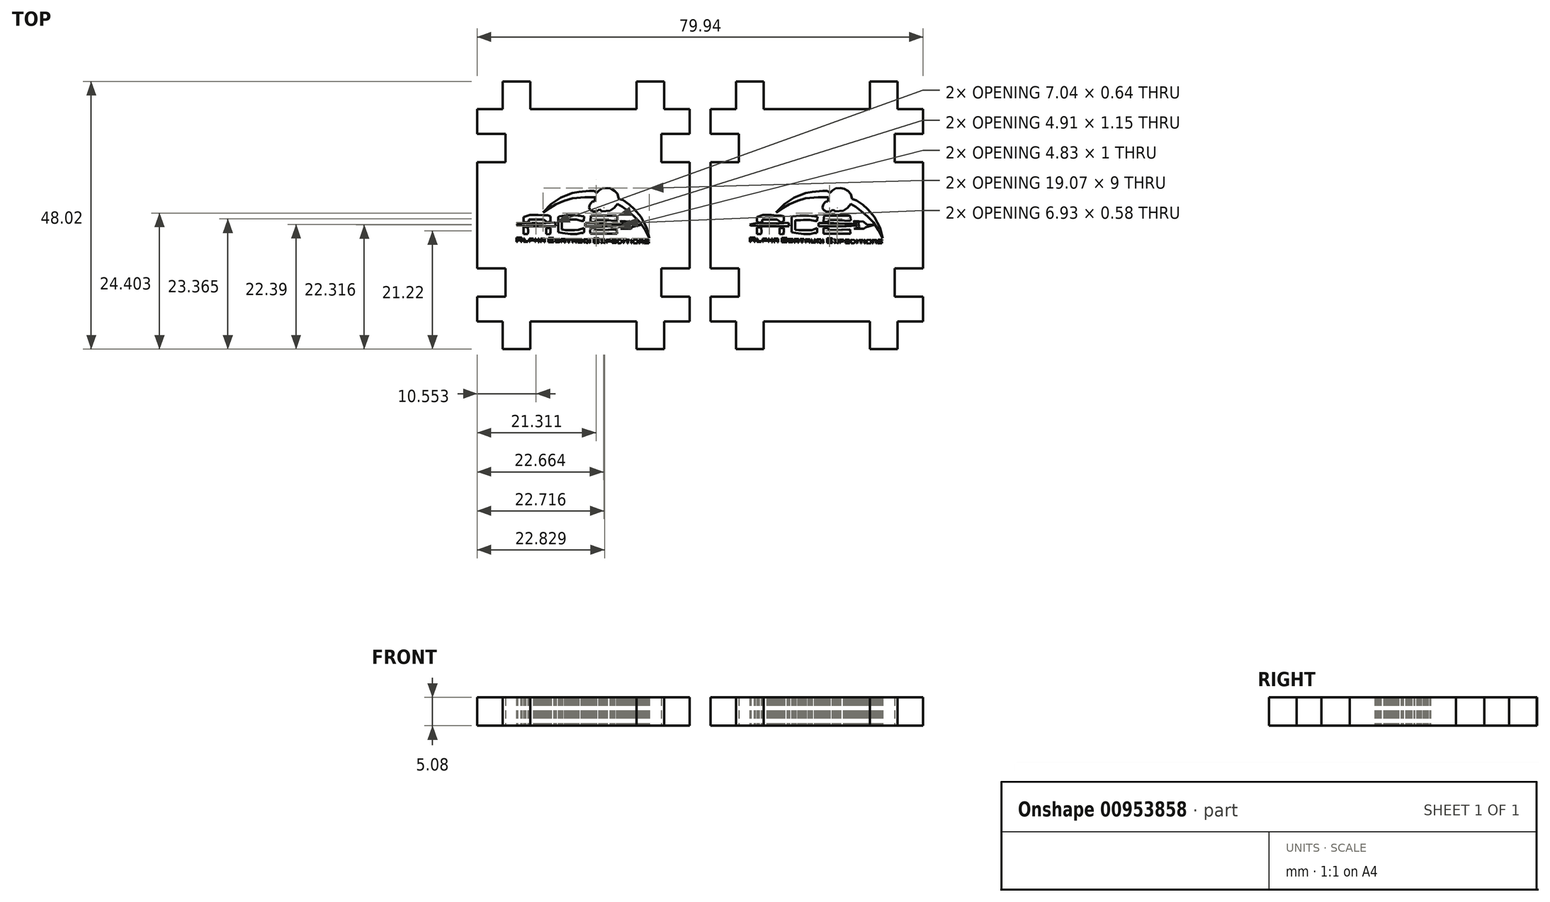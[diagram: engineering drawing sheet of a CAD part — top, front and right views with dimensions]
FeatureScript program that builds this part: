
annotation { "Feature Type Name" : "Feature", "Feature Type Description" : "" }
export const myFeature = defineFeature(function(context is Context, id is Id, definition is map)
    precondition{}
    {
        {
            var Q0;
            Q0=qCreatedBy(makeId("Top.planeOp"),FACE);
            var sketch = newSketch(context, id + "F0", { "sketchPlane" : qUnion([Q0])});
            skLineSegment(sketch, "E0.top", {"start": v(-44, -7.5) * mm, "end": v(-39.42, -7.5) * mm});
            skLineSegment(sketch, "E0.right", {"start": v(-5.9, 30.6) * mm, "end": v(-5.9, -7.5) * mm});
            skPoint(sketch, "E0.middle", {"position": v(-24.95, 11.56) * mm});
            skLineSegment(sketch, "E1", {"start": v(-44, 30.6) * mm, "end": v(-44, 11.56) * mm});
            skLineSegment(sketch, "E2", {"start": v(-44, 11.56) * mm, "end": v(-44, -7.5) * mm});
            skLineSegment(sketch, "E3", {"start": v(-44, 21.08) * mm, "end": v(-38.92, 21.08) * mm});
            skLineSegment(sketch, "E4", {"start": v(-38.92, 21.08) * mm, "end": v(-38.92, 26.16) * mm});
            skLineSegment(sketch, "E5", {"start": v(-38.92, 26.16) * mm, "end": v(-44, 26.16) * mm});
            skLineSegment(sketch, "E6.MirrorCS", {"start": v(-44, 2.03) * mm, "end": v(-38.92, 2.03) * mm});
            skLineSegment(sketch, "E7.MirrorCS", {"start": v(-38.92, 2.03) * mm, "end": v(-38.92, -3.05) * mm});
            skLineSegment(sketch, "E8.MirrorCS", {"start": v(-38.92, -3.05) * mm, "end": v(-44, -3.05) * mm});
            skLineSegment(sketch, "E9.MirrorCS", {"start": v(-10.98, 21.08) * mm, "end": v(-10.98, 26.16) * mm});
            skLineSegment(sketch, "E10.MirrorCS", {"start": v(-10.98, 26.16) * mm, "end": v(-5.9, 26.16) * mm});
            skLineSegment(sketch, "E11.MirrorCS", {"start": v(-5.9, 21.08) * mm, "end": v(-10.98, 21.08) * mm});
            skLineSegment(sketch, "E12.MirrorCS", {"start": v(-5.9, 2.03) * mm, "end": v(-10.98, 2.03) * mm});
            skLineSegment(sketch, "E13.MirrorCS", {"start": v(-10.98, 2.03) * mm, "end": v(-10.98, -3.05) * mm});
            skLineSegment(sketch, "E14.MirrorCS", {"start": v(-10.98, -3.05) * mm, "end": v(-5.9, -3.05) * mm});
            skLineSegment(sketch, "E15", {"start": v(-44, 30.6) * mm, "end": v(-39.42, 30.6) * mm});
            skLineSegment(sketch, "E16", {"start": v(-24.95, 30.6) * mm, "end": v(-15.42, 30.6) * mm});
            skLineSegment(sketch, "E17", {"start": v(-34.47, 30.6) * mm, "end": v(-34.47, 35.56) * mm});
            skLineSegment(sketch, "E18", {"start": v(-34.47, 35.56) * mm, "end": v(-39.42, 35.56) * mm});
            skLineSegment(sketch, "E19", {"start": v(-39.42, 35.56) * mm, "end": v(-39.42, 30.6) * mm});
            skLineSegment(sketch, "E20", {"start": v(-15.42, 30.6) * mm, "end": v(-15.42, 35.56) * mm});
            skLineSegment(sketch, "E21", {"start": v(-15.42, 35.56) * mm, "end": v(-10.47, 35.56) * mm});
            skLineSegment(sketch, "E22", {"start": v(-10.47, 35.56) * mm, "end": v(-10.47, 30.6) * mm});
            skLineSegment(sketch, "E23.MirrorCS", {"start": v(-34.47, -7.5) * mm, "end": v(-34.47, -12.44) * mm});
            skLineSegment(sketch, "E24.MirrorCS", {"start": v(-34.47, -12.44) * mm, "end": v(-39.42, -12.44) * mm});
            skLineSegment(sketch, "E25.MirrorCS", {"start": v(-39.42, -12.44) * mm, "end": v(-39.42, -7.5) * mm});
            skLineSegment(sketch, "E26.MirrorCS", {"start": v(-15.42, -7.5) * mm, "end": v(-15.42, -12.44) * mm});
            skLineSegment(sketch, "E27.MirrorCS", {"start": v(-15.42, -12.44) * mm, "end": v(-10.47, -12.44) * mm});
            skLineSegment(sketch, "E28.MirrorCS", {"start": v(-10.47, -12.44) * mm, "end": v(-10.47, -7.5) * mm});
            skLineSegment(sketch, "E29.trimOffspring", {"start": v(-34.47, 30.6) * mm, "end": v(-24.95, 30.6) * mm});
            skLineSegment(sketch, "E30.trimOffspring", {"start": v(-10.47, 30.6) * mm, "end": v(-5.9, 30.6) * mm});
            skLineSegment(sketch, "E31.trimOffspring", {"start": v(-34.47, -7.5) * mm, "end": v(-15.42, -7.5) * mm});
            skLineSegment(sketch, "E32.trimOffspring", {"start": v(-10.47, -7.5) * mm, "end": v(-5.9, -7.5) * mm});
            skPoint(sketch, "E33.endSnap0", {"position": v(-13.11, 17.66) * mm});
            skLineSegment(sketch, "E34", {"start": v(-35.7, 10.44) * mm, "end": v(-35.7, 11.26) * mm});
            skLineSegment(sketch, "E35", {"start": v(-35.7, 11.26) * mm, "end": v(-34.58, 11.6) * mm});
            skLineSegment(sketch, "E36", {"start": v(-34.58, 11.6) * mm, "end": v(-33.1, 11.6) * mm});
            skLineSegment(sketch, "E37", {"start": v(-33.1, 11.6) * mm, "end": v(-32.18, 11.52) * mm});
            skLineSegment(sketch, "E38", {"start": v(-32.18, 11.52) * mm, "end": v(-31.36, 11.52) * mm});
            skLineSegment(sketch, "E39", {"start": v(-31.36, 11.52) * mm, "end": v(-30.88, 11.38) * mm});
            skLineSegment(sketch, "E40", {"start": v(-30.88, 11.38) * mm, "end": v(-30.88, 10.48) * mm});
            skLineSegment(sketch, "E41", {"start": v(-30.88, 10.48) * mm, "end": v(-31.36, 10.3) * mm});
            skLineSegment(sketch, "E42", {"start": v(-31.36, 10.3) * mm, "end": v(-31.75, 10.57) * mm});
            skLineSegment(sketch, "E43", {"start": v(-31.75, 10.57) * mm, "end": v(-32.06, 10.77) * mm});
            skLineSegment(sketch, "E44", {"start": v(-32.06, 10.77) * mm, "end": v(-34.73, 10.77) * mm});
            skLineSegment(sketch, "E45", {"start": v(-34.73, 10.77) * mm, "end": v(-34.73, 10.38) * mm});
            skLineSegment(sketch, "E46", {"start": v(-34.73, 10.38) * mm, "end": v(-35.32, 10.26) * mm});
            skLineSegment(sketch, "E47", {"start": v(-35.32, 10.26) * mm, "end": v(-35.7, 10.44) * mm});
            skLineSegment(sketch, "E48", {"start": v(-36.97, 9.95) * mm, "end": v(-35.7, 10.17) * mm});
            skLineSegment(sketch, "E49", {"start": v(-35.7, 10.17) * mm, "end": v(-34.75, 10.17) * mm});
            skLineSegment(sketch, "E50", {"start": v(-34.75, 10.17) * mm, "end": v(-33.34, 10.13) * mm});
            skLineSegment(sketch, "E51", {"start": v(-33.34, 10.13) * mm, "end": v(-31.7, 10.13) * mm});
            skLineSegment(sketch, "E52", {"start": v(-31.7, 10.13) * mm, "end": v(-30.06, 10.25) * mm});
            skLineSegment(sketch, "E53", {"start": v(-30.06, 10.25) * mm, "end": v(-29.93, 9.6) * mm});
            skLineSegment(sketch, "E54", {"start": v(-29.93, 9.6) * mm, "end": v(-34.95, 9.6) * mm});
            skLineSegment(sketch, "E55", {"start": v(-34.95, 9.6) * mm, "end": v(-35.99, 9.74) * mm});
            skLineSegment(sketch, "E56", {"start": v(-35.99, 9.74) * mm, "end": v(-36.8, 9.74) * mm});
            skLineSegment(sketch, "E57", {"start": v(-36.8, 9.74) * mm, "end": v(-36.97, 9.95) * mm});
            skLineSegment(sketch, "E58", {"start": v(-35.7, 9.42) * mm, "end": v(-35.7, 8.41) * mm});
            skLineSegment(sketch, "E59", {"start": v(-35.7, 8.41) * mm, "end": v(-35.7, 8.17) * mm});
            skLineSegment(sketch, "E60", {"start": v(-35.7, 8.17) * mm, "end": v(-34.95, 8.17) * mm});
            skLineSegment(sketch, "E61", {"start": v(-34.95, 8.17) * mm, "end": v(-34.84, 8.6) * mm});
            skLineSegment(sketch, "E62", {"start": v(-34.84, 8.6) * mm, "end": v(-34.95, 9.42) * mm});
            skLineSegment(sketch, "E63", {"start": v(-34.95, 9.42) * mm, "end": v(-35.7, 9.42) * mm});
            skLineSegment(sketch, "E64", {"start": v(-31.62, 9.26) * mm, "end": v(-31.62, 8.17) * mm});
            skLineSegment(sketch, "E65", {"start": v(-31.62, 8.17) * mm, "end": v(-31.01, 8.13) * mm});
            skLineSegment(sketch, "E66", {"start": v(-31.01, 8.13) * mm, "end": v(-30.86, 8.48) * mm});
            skLineSegment(sketch, "E67", {"start": v(-30.86, 8.48) * mm, "end": v(-30.86, 9.25) * mm});
            skLineSegment(sketch, "E68", {"start": v(-30.86, 9.25) * mm, "end": v(-31.62, 9.26) * mm});
            skLineSegment(sketch, "E69", {"start": v(-29.46, 11.22) * mm, "end": v(-29.46, 8.52) * mm});
            skLineSegment(sketch, "E70", {"start": v(-29.46, 8.52) * mm, "end": v(-28.7, 8.36) * mm});
            skLineSegment(sketch, "E71", {"start": v(-28.7, 8.36) * mm, "end": v(-27.32, 8.2) * mm});
            skLineSegment(sketch, "E72", {"start": v(-27.32, 8.2) * mm, "end": v(-26.16, 8.2) * mm});
            skLineSegment(sketch, "E73", {"start": v(-26.16, 8.2) * mm, "end": v(-25.39, 8.37) * mm});
            skLineSegment(sketch, "E74", {"start": v(-25.39, 8.37) * mm, "end": v(-24.97, 8.37) * mm});
            skLineSegment(sketch, "E75", {"start": v(-24.97, 8.37) * mm, "end": v(-24.86, 8.64) * mm});
            skLineSegment(sketch, "E76", {"start": v(-24.86, 8.64) * mm, "end": v(-24.86, 9.26) * mm});
            skLineSegment(sketch, "E77", {"start": v(-24.86, 9.26) * mm, "end": v(-25.86, 8.93) * mm});
            skLineSegment(sketch, "E78", {"start": v(-25.86, 8.93) * mm, "end": v(-26.53, 8.87) * mm});
            skLineSegment(sketch, "E79", {"start": v(-26.53, 8.87) * mm, "end": v(-27, 8.87) * mm});
            skLineSegment(sketch, "E80", {"start": v(-27, 8.87) * mm, "end": v(-28.15, 8.87) * mm});
            skLineSegment(sketch, "E81", {"start": v(-28.15, 8.87) * mm, "end": v(-28.8, 8.98) * mm});
            skLineSegment(sketch, "E82", {"start": v(-28.8, 8.98) * mm, "end": v(-28.8, 9.42) * mm});
            skLineSegment(sketch, "E83", {"start": v(-28.8, 9.42) * mm, "end": v(-28.8, 10.22) * mm});
            skLineSegment(sketch, "E84", {"start": v(-28.8, 10.22) * mm, "end": v(-28.8, 10.7) * mm});
            skLineSegment(sketch, "E85", {"start": v(-28.8, 10.7) * mm, "end": v(-27.88, 10.7) * mm});
            skLineSegment(sketch, "E86", {"start": v(-27.88, 10.7) * mm, "end": v(-27.34, 10.76) * mm});
            skLineSegment(sketch, "E87", {"start": v(-27.34, 10.76) * mm, "end": v(-26.2, 10.76) * mm});
            skLineSegment(sketch, "E88", {"start": v(-26.2, 10.76) * mm, "end": v(-25.3, 10.55) * mm});
            skLineSegment(sketch, "E89", {"start": v(-25.3, 10.55) * mm, "end": v(-24.9, 10.55) * mm});
            skLineSegment(sketch, "E90", {"start": v(-24.9, 10.55) * mm, "end": v(-24.8, 11.33) * mm});
            skLineSegment(sketch, "E91", {"start": v(-24.8, 11.33) * mm, "end": v(-26.44, 11.53) * mm});
            skLineSegment(sketch, "E92", {"start": v(-26.44, 11.53) * mm, "end": v(-28, 11.53) * mm});
            skLineSegment(sketch, "E93", {"start": v(-28, 11.53) * mm, "end": v(-29.29, 11.36) * mm});
            skLineSegment(sketch, "E94", {"start": v(-29.29, 11.36) * mm, "end": v(-29.46, 11.22) * mm});
            skLineSegment(sketch, "E95", {"start": v(-24.64, 10.14) * mm, "end": v(-24.64, 9.57) * mm});
            skLineSegment(sketch, "E96", {"start": v(-24.64, 9.57) * mm, "end": v(-19.66, 9.57) * mm});
            skLineSegment(sketch, "E97", {"start": v(-19.66, 9.57) * mm, "end": v(-18.62, 9.67) * mm});
            skLineSegment(sketch, "E98", {"start": v(-18.62, 9.67) * mm, "end": v(-17.7, 9.75) * mm});
            skLineSegment(sketch, "E99", {"start": v(-17.7, 9.75) * mm, "end": v(-17.7, 9.9) * mm});
            skLineSegment(sketch, "E100", {"start": v(-17.7, 9.9) * mm, "end": v(-18.68, 10.05) * mm});
            skLineSegment(sketch, "E101", {"start": v(-18.68, 10.05) * mm, "end": v(-20.12, 10.05) * mm});
            skLineSegment(sketch, "E102", {"start": v(-20.12, 10.05) * mm, "end": v(-21.88, 10.14) * mm});
            skLineSegment(sketch, "E103", {"start": v(-21.88, 10.14) * mm, "end": v(-24.64, 10.14) * mm});
            skLineSegment(sketch, "E104", {"start": v(-23.71, 10.55) * mm, "end": v(-23.63, 11.48) * mm});
            skLineSegment(sketch, "E105", {"start": v(-23.63, 11.48) * mm, "end": v(-19.03, 11.48) * mm});
            skLineSegment(sketch, "E106", {"start": v(-19.03, 11.48) * mm, "end": v(-18.89, 11.33) * mm});
            skLineSegment(sketch, "E107", {"start": v(-18.89, 11.33) * mm, "end": v(-18.83, 10.7) * mm});
            skLineSegment(sketch, "E108", {"start": v(-18.83, 10.7) * mm, "end": v(-19.05, 10.55) * mm});
            skLineSegment(sketch, "E109", {"start": v(-19.05, 10.55) * mm, "end": v(-21.94, 10.7) * mm});
            skLineSegment(sketch, "E110", {"start": v(-21.94, 10.7) * mm, "end": v(-22.76, 10.7) * mm});
            skLineSegment(sketch, "E111", {"start": v(-22.76, 10.7) * mm, "end": v(-22.81, 10.33) * mm});
            skLineSegment(sketch, "E112", {"start": v(-22.81, 10.33) * mm, "end": v(-23.38, 10.33) * mm});
            skLineSegment(sketch, "E113", {"start": v(-23.38, 10.33) * mm, "end": v(-23.74, 10.44) * mm});
            skLineSegment(sketch, "E114", {"start": v(-23.74, 10.44) * mm, "end": v(-23.71, 10.55) * mm});
            skLineSegment(sketch, "E115", {"start": v(-23.71, 9.26) * mm, "end": v(-22.94, 9.26) * mm});
            skLineSegment(sketch, "E116", {"start": v(-22.94, 9.26) * mm, "end": v(-22.8, 8.92) * mm});
            skLineSegment(sketch, "E117", {"start": v(-22.8, 8.92) * mm, "end": v(-22.1, 8.9) * mm});
            skLineSegment(sketch, "E118", {"start": v(-22.1, 8.9) * mm, "end": v(-19, 9) * mm});
            skLineSegment(sketch, "E119", {"start": v(-19, 9) * mm, "end": v(-18.92, 8.26) * mm});
            skLineSegment(sketch, "E120", {"start": v(-18.92, 8.26) * mm, "end": v(-23.47, 8.26) * mm});
            skLineSegment(sketch, "E121", {"start": v(-23.47, 8.26) * mm, "end": v(-23.71, 8.26) * mm});
            skLineSegment(sketch, "E122", {"start": v(-23.71, 8.26) * mm, "end": v(-23.75, 8.65) * mm});
            skLineSegment(sketch, "E123", {"start": v(-23.75, 8.65) * mm, "end": v(-23.71, 9.26) * mm});
            skLineSegment(sketch, "E124", {"start": v(-18.21, 10.55) * mm, "end": v(-16.54, 10.44) * mm});
            skLineSegment(sketch, "E125", {"start": v(-16.54, 10.44) * mm, "end": v(-16, 9.95) * mm});
            skLineSegment(sketch, "E126", {"start": v(-16, 9.95) * mm, "end": v(-14.66, 9.82) * mm});
            skLineSegment(sketch, "E127", {"start": v(-14.66, 9.82) * mm, "end": v(-16.19, 9.42) * mm});
            skLineSegment(sketch, "E128", {"start": v(-16.19, 9.42) * mm, "end": v(-16.47, 9.13) * mm});
            skLineSegment(sketch, "E129", {"start": v(-16.47, 9.13) * mm, "end": v(-18.28, 9.13) * mm});
            skLineSegment(sketch, "E130", {"start": v(-18.28, 9.13) * mm, "end": v(-17.4, 9.42) * mm});
            skLineSegment(sketch, "E131", {"start": v(-17.4, 9.42) * mm, "end": v(-17.3, 9.62) * mm});
            skLineSegment(sketch, "E132", {"start": v(-17.3, 9.62) * mm, "end": v(-17.48, 9.83) * mm});
            skLineSegment(sketch, "E133", {"start": v(-17.48, 9.83) * mm, "end": v(-17.3, 10.04) * mm});
            skLineSegment(sketch, "E134", {"start": v(-17.3, 10.04) * mm, "end": v(-17.66, 10.32) * mm});
            skLineSegment(sketch, "E135", {"start": v(-17.66, 10.32) * mm, "end": v(-18.25, 10.37) * mm});
            skLineSegment(sketch, "E136", {"start": v(-18.25, 10.37) * mm, "end": v(-18.38, 10.44) * mm});
            skLineSegment(sketch, "E137", {"start": v(-18.38, 10.44) * mm, "end": v(-18.21, 10.55) * mm});
            skLineSegment(sketch, "E138", {"start": v(-18.85, 13.59) * mm, "end": v(-17.99, 13.1) * mm});
            skLineSegment(sketch, "E139", {"start": v(-17.99, 13.1) * mm, "end": v(-17, 12.35) * mm});
            skLineSegment(sketch, "E140", {"start": v(-17, 12.35) * mm, "end": v(-15.89, 11.39) * mm});
            skLineSegment(sketch, "E141", {"start": v(-15.89, 11.39) * mm, "end": v(-14.8, 10.3) * mm});
            skLineSegment(sketch, "E142", {"start": v(-14.8, 10.3) * mm, "end": v(-13.88, 8.92) * mm});
            skLineSegment(sketch, "E143", {"start": v(-13.88, 8.92) * mm, "end": v(-13.16, 7.44) * mm});
            skLineSegment(sketch, "E144", {"start": v(-13.16, 7.44) * mm, "end": v(-13.57, 9.26) * mm});
            skLineSegment(sketch, "E145", {"start": v(-13.57, 9.26) * mm, "end": v(-14.1, 10.2) * mm});
            skLineSegment(sketch, "E146", {"start": v(-14.1, 10.2) * mm, "end": v(-14.6, 11.22) * mm});
            skLineSegment(sketch, "E147", {"start": v(-14.6, 11.22) * mm, "end": v(-15.8, 12.65) * mm});
            skLineSegment(sketch, "E148", {"start": v(-15.8, 12.65) * mm, "end": v(-16.72, 13.48) * mm});
            skLineSegment(sketch, "E149", {"start": v(-16.72, 13.48) * mm, "end": v(-17.85, 14.26) * mm});
            skLineSegment(sketch, "E150", {"start": v(-17.85, 14.26) * mm, "end": v(-18.6, 14.48) * mm});
            skLineSegment(sketch, "E151", {"start": v(-18.6, 14.48) * mm, "end": v(-18.85, 13.59) * mm});
            skLineSegment(sketch, "E152", {"start": v(-18.85, 13.59) * mm, "end": v(-19.4, 12.91) * mm});
            skLineSegment(sketch, "E153", {"start": v(-19.4, 12.91) * mm, "end": v(-20.2, 12.4) * mm});
            skLineSegment(sketch, "E154", {"start": v(-20.2, 12.4) * mm, "end": v(-21.65, 12.26) * mm});
            skLineSegment(sketch, "E155", {"start": v(-21.65, 12.26) * mm, "end": v(-22.02, 12.6) * mm});
            skLineSegment(sketch, "E156", {"start": v(-22.02, 12.6) * mm, "end": v(-22.6, 12.22) * mm});
            skLineSegment(sketch, "E157", {"start": v(-22.6, 12.22) * mm, "end": v(-23.18, 12.23) * mm});
            skLineSegment(sketch, "E158", {"start": v(-23.18, 12.23) * mm, "end": v(-23.6, 12.43) * mm});
            skLineSegment(sketch, "E159", {"start": v(-23.6, 12.43) * mm, "end": v(-23.83, 12.65) * mm});
            skLineSegment(sketch, "E160", {"start": v(-23.83, 12.65) * mm, "end": v(-23.94, 12.93) * mm});
            skLineSegment(sketch, "E161", {"start": v(-23.94, 12.93) * mm, "end": v(-23.8, 13.47) * mm});
            skLineSegment(sketch, "E162", {"start": v(-23.8, 13.47) * mm, "end": v(-23.58, 13.76) * mm});
            skLineSegment(sketch, "E163", {"start": v(-23.58, 13.76) * mm, "end": v(-23.4, 14) * mm});
            skLineSegment(sketch, "E164", {"start": v(-23.4, 14) * mm, "end": v(-23.06, 14.05) * mm});
            skLineSegment(sketch, "E165", {"start": v(-23.06, 14.05) * mm, "end": v(-22.6, 13.99) * mm});
            skLineSegment(sketch, "E166", {"start": v(-22.6, 13.99) * mm, "end": v(-22.27, 13.8) * mm});
            skLineSegment(sketch, "E167", {"start": v(-22.27, 13.8) * mm, "end": v(-21.99, 13.38) * mm});
            skLineSegment(sketch, "E168", {"start": v(-21.99, 13.38) * mm, "end": v(-21.95, 13.14) * mm});
            skLineSegment(sketch, "E169", {"start": v(-21.95, 13.14) * mm, "end": v(-21.95, 12.78) * mm});
            skLineSegment(sketch, "E170", {"start": v(-21.95, 12.78) * mm, "end": v(-22.02, 12.6) * mm});
            skLineSegment(sketch, "E171", {"start": v(-22.97, 14.04) * mm, "end": v(-22.9, 14.6) * mm});
            skLineSegment(sketch, "E172", {"start": v(-22.9, 14.6) * mm, "end": v(-22.6, 15.54) * mm});
            skLineSegment(sketch, "E173", {"start": v(-22.6, 15.54) * mm, "end": v(-22.17, 16) * mm});
            skLineSegment(sketch, "E174", {"start": v(-22.17, 16) * mm, "end": v(-21.6, 16.38) * mm});
            skLineSegment(sketch, "E175", {"start": v(-21.6, 16.38) * mm, "end": v(-20.72, 16.45) * mm});
            skLineSegment(sketch, "E176", {"start": v(-20.72, 16.45) * mm, "end": v(-20.06, 16.35) * mm});
            skLineSegment(sketch, "E177", {"start": v(-20.06, 16.35) * mm, "end": v(-19.39, 15.95) * mm});
            skLineSegment(sketch, "E178", {"start": v(-19.39, 15.95) * mm, "end": v(-18.85, 15.4) * mm});
            skLineSegment(sketch, "E179", {"start": v(-18.85, 15.4) * mm, "end": v(-18.65, 14.7) * mm});
            skLineSegment(sketch, "E180", {"start": v(-18.65, 14.7) * mm, "end": v(-18.6, 14.48) * mm});
            skLineSegment(sketch, "E181", {"start": v(-22.6, 15.54) * mm, "end": v(-23.01, 15.94) * mm});
            skLineSegment(sketch, "E182", {"start": v(-23.01, 15.94) * mm, "end": v(-23.87, 15.95) * mm});
            skLineSegment(sketch, "E183", {"start": v(-23.87, 15.95) * mm, "end": v(-25.77, 15.75) * mm});
            skLineSegment(sketch, "E184", {"start": v(-25.77, 15.75) * mm, "end": v(-26.94, 15.54) * mm});
            skLineSegment(sketch, "E185", {"start": v(-26.94, 15.54) * mm, "end": v(-28.04, 15.12) * mm});
            skLineSegment(sketch, "E186", {"start": v(-28.04, 15.12) * mm, "end": v(-29.04, 14.71) * mm});
            skLineSegment(sketch, "E187", {"start": v(-29.04, 14.71) * mm, "end": v(-30.75, 13.59) * mm});
            skLineSegment(sketch, "E188", {"start": v(-30.75, 13.59) * mm, "end": v(-32.04, 12.26) * mm});
            skLineSegment(sketch, "E189", {"start": v(-32.04, 12.26) * mm, "end": v(-32.22, 12.07) * mm});
            skLineSegment(sketch, "E190", {"start": v(-32.22, 12.07) * mm, "end": v(-30.95, 12.9) * mm});
            skLineSegment(sketch, "E191", {"start": v(-30.95, 12.9) * mm, "end": v(-29.88, 13.52) * mm});
            skLineSegment(sketch, "E192", {"start": v(-29.88, 13.52) * mm, "end": v(-28.4, 14.14) * mm});
            skLineSegment(sketch, "E193", {"start": v(-28.4, 14.14) * mm, "end": v(-26.96, 14.6) * mm});
            skLineSegment(sketch, "E194", {"start": v(-26.96, 14.6) * mm, "end": v(-24.7, 14.82) * mm});
            skLineSegment(sketch, "E195", {"start": v(-24.7, 14.82) * mm, "end": v(-22.82, 14.82) * mm});
            skLineSegment(sketch, "E196", {"start": v(-36.97, 6.8) * mm, "end": v(-36.97, 7.57) * mm});
            skLineSegment(sketch, "E197", {"start": v(-36.97, 7.57) * mm, "end": v(-36, 7.57) * mm});
            skLineSegment(sketch, "E198", {"start": v(-36, 7.57) * mm, "end": v(-36, 6.78) * mm});
            skLineSegment(sketch, "E199", {"start": v(-36, 6.78) * mm, "end": v(-36.18, 6.78) * mm});
            skLineSegment(sketch, "E200", {"start": v(-36.18, 6.78) * mm, "end": v(-36.18, 7.1) * mm});
            skLineSegment(sketch, "E201", {"start": v(-36.18, 7.1) * mm, "end": v(-36.77, 7.1) * mm});
            skLineSegment(sketch, "E202", {"start": v(-36.77, 7.1) * mm, "end": v(-36.77, 6.78) * mm});
            skLineSegment(sketch, "E203", {"start": v(-36.77, 6.78) * mm, "end": v(-36.97, 6.8) * mm});
            skLineSegment(sketch, "E204", {"start": v(-36.79, 7.39) * mm, "end": v(-36.79, 7.28) * mm});
            skLineSegment(sketch, "E205", {"start": v(-36.79, 7.28) * mm, "end": v(-36.2, 7.28) * mm});
            skLineSegment(sketch, "E206", {"start": v(-36.2, 7.28) * mm, "end": v(-36.2, 7.39) * mm});
            skLineSegment(sketch, "E207", {"start": v(-36.2, 7.39) * mm, "end": v(-36.79, 7.39) * mm});
            skLineSegment(sketch, "E208", {"start": v(-35.7, 7.39) * mm, "end": v(-35.7, 6.77) * mm});
            skLineSegment(sketch, "E209", {"start": v(-35.7, 6.77) * mm, "end": v(-34.94, 6.77) * mm});
            skLineSegment(sketch, "E210", {"start": v(-34.94, 6.77) * mm, "end": v(-34.94, 6.9) * mm});
            skLineSegment(sketch, "E211", {"start": v(-34.94, 6.9) * mm, "end": v(-35.53, 6.9) * mm});
            skLineSegment(sketch, "E212", {"start": v(-35.53, 6.9) * mm, "end": v(-35.53, 7.39) * mm});
            skLineSegment(sketch, "E213", {"start": v(-35.53, 7.39) * mm, "end": v(-35.7, 7.39) * mm});
            skLineSegment(sketch, "E214", {"start": v(-34.68, 6.8) * mm, "end": v(-34.68, 7.39) * mm});
            skLineSegment(sketch, "E215", {"start": v(-34.68, 7.39) * mm, "end": v(-33.92, 7.39) * mm});
            skLineSegment(sketch, "E216", {"start": v(-33.92, 7.39) * mm, "end": v(-33.92, 7.01) * mm});
            skLineSegment(sketch, "E217", {"start": v(-33.92, 7.01) * mm, "end": v(-34.53, 7.01) * mm});
            skLineSegment(sketch, "E218", {"start": v(-34.53, 7.01) * mm, "end": v(-34.53, 6.8) * mm});
            skLineSegment(sketch, "E219", {"start": v(-34.53, 6.8) * mm, "end": v(-34.68, 6.8) * mm});
            skLineSegment(sketch, "E220", {"start": v(-34.54, 7.26) * mm, "end": v(-34.54, 7.1) * mm});
            skLineSegment(sketch, "E221", {"start": v(-34.54, 7.1) * mm, "end": v(-34.07, 7.1) * mm});
            skLineSegment(sketch, "E222", {"start": v(-34.07, 7.1) * mm, "end": v(-34.07, 7.25) * mm});
            skLineSegment(sketch, "E223", {"start": v(-34.07, 7.25) * mm, "end": v(-34.54, 7.26) * mm});
            skLineSegment(sketch, "E224", {"start": v(-33.67, 7.39) * mm, "end": v(-33.67, 6.8) * mm});
            skLineSegment(sketch, "E225", {"start": v(-33.67, 6.8) * mm, "end": v(-33.51, 6.8) * mm});
            skLineSegment(sketch, "E226", {"start": v(-33.51, 6.8) * mm, "end": v(-33.52, 6.99) * mm});
            skLineSegment(sketch, "E227", {"start": v(-33.52, 6.99) * mm, "end": v(-33.04, 6.99) * mm});
            skLineSegment(sketch, "E228", {"start": v(-33.04, 6.99) * mm, "end": v(-33.06, 6.75) * mm});
            skLineSegment(sketch, "E229", {"start": v(-33.06, 6.75) * mm, "end": v(-32.9, 6.75) * mm});
            skLineSegment(sketch, "E230", {"start": v(-32.9, 6.75) * mm, "end": v(-32.9, 7.39) * mm});
            skLineSegment(sketch, "E231", {"start": v(-32.9, 7.39) * mm, "end": v(-33.08, 7.39) * mm});
            skLineSegment(sketch, "E232", {"start": v(-33.08, 7.39) * mm, "end": v(-33.08, 7.14) * mm});
            skLineSegment(sketch, "E233", {"start": v(-33.08, 7.14) * mm, "end": v(-33.47, 7.14) * mm});
            skLineSegment(sketch, "E234", {"start": v(-33.47, 7.14) * mm, "end": v(-33.47, 7.39) * mm});
            skLineSegment(sketch, "E235", {"start": v(-33.47, 7.39) * mm, "end": v(-33.67, 7.39) * mm});
            skLineSegment(sketch, "E236", {"start": v(-32.65, 6.76) * mm, "end": v(-32.65, 7.39) * mm});
            skLineSegment(sketch, "E237", {"start": v(-32.65, 7.39) * mm, "end": v(-31.88, 7.39) * mm});
            skLineSegment(sketch, "E238", {"start": v(-31.88, 7.39) * mm, "end": v(-31.88, 6.73) * mm});
            skLineSegment(sketch, "E239", {"start": v(-31.88, 6.73) * mm, "end": v(-32.02, 6.73) * mm});
            skLineSegment(sketch, "E240", {"start": v(-32.02, 6.73) * mm, "end": v(-32, 6.96) * mm});
            skLineSegment(sketch, "E241", {"start": v(-32, 6.96) * mm, "end": v(-32.48, 6.96) * mm});
            skLineSegment(sketch, "E242", {"start": v(-32.48, 6.96) * mm, "end": v(-32.47, 6.74) * mm});
            skLineSegment(sketch, "E243", {"start": v(-32.47, 6.74) * mm, "end": v(-32.65, 6.76) * mm});
            skLineSegment(sketch, "E244", {"start": v(-32.48, 7.22) * mm, "end": v(-32.48, 7.1) * mm});
            skLineSegment(sketch, "E245", {"start": v(-32.48, 7.1) * mm, "end": v(-32.04, 7.11) * mm});
            skLineSegment(sketch, "E246", {"start": v(-32.04, 7.11) * mm, "end": v(-32.06, 7.24) * mm});
            skLineSegment(sketch, "E247", {"start": v(-32.06, 7.24) * mm, "end": v(-32.48, 7.22) * mm});
            skLineSegment(sketch, "E248", {"start": v(-31.26, 7.52) * mm, "end": v(-31.26, 6.73) * mm});
            skLineSegment(sketch, "E249", {"start": v(-31.26, 6.73) * mm, "end": v(-30.28, 6.73) * mm});
            skLineSegment(sketch, "E250", {"start": v(-30.28, 6.73) * mm, "end": v(-30.28, 6.89) * mm});
            skLineSegment(sketch, "E251", {"start": v(-30.28, 6.89) * mm, "end": v(-31.01, 6.89) * mm});
            skLineSegment(sketch, "E252", {"start": v(-31.01, 6.89) * mm, "end": v(-31.01, 7.32) * mm});
            skLineSegment(sketch, "E253", {"start": v(-31.01, 7.32) * mm, "end": v(-30.28, 7.32) * mm});
            skLineSegment(sketch, "E254", {"start": v(-30.28, 7.32) * mm, "end": v(-30.28, 7.5) * mm});
            skLineSegment(sketch, "E255", {"start": v(-30.28, 7.5) * mm, "end": v(-31.26, 7.5) * mm});
            skLineSegment(sketch, "E256", {"start": v(-30, 7.32) * mm, "end": v(-30, 6.72) * mm});
            skLineSegment(sketch, "E257", {"start": v(-30, 6.72) * mm, "end": v(-29.25, 6.72) * mm});
            skLineSegment(sketch, "E258", {"start": v(-29.25, 6.72) * mm, "end": v(-29.24, 6.8) * mm});
            skLineSegment(sketch, "E259", {"start": v(-29.24, 6.8) * mm, "end": v(-29.84, 6.8) * mm});
            skLineSegment(sketch, "E260", {"start": v(-29.84, 6.8) * mm, "end": v(-29.84, 6.92) * mm});
            skLineSegment(sketch, "E261", {"start": v(-29.84, 6.92) * mm, "end": v(-29.24, 6.92) * mm});
            skLineSegment(sketch, "E262", {"start": v(-29.24, 6.92) * mm, "end": v(-29.24, 7.07) * mm});
            skLineSegment(sketch, "E263", {"start": v(-29.24, 7.07) * mm, "end": v(-29.83, 7.07) * mm});
            skLineSegment(sketch, "E264", {"start": v(-29.83, 7.07) * mm, "end": v(-29.83, 7.2) * mm});
            skLineSegment(sketch, "E265", {"start": v(-29.83, 7.2) * mm, "end": v(-29.2, 7.2) * mm});
            skLineSegment(sketch, "E266", {"start": v(-29.2, 7.2) * mm, "end": v(-29.2, 7.34) * mm});
            skLineSegment(sketch, "E267", {"start": v(-29.2, 7.34) * mm, "end": v(-30, 7.32) * mm});
            skLineSegment(sketch, "E268", {"start": v(-28.98, 7.32) * mm, "end": v(-28.98, 6.7) * mm});
            skLineSegment(sketch, "E269", {"start": v(-28.98, 6.7) * mm, "end": v(-28.83, 6.7) * mm});
            skLineSegment(sketch, "E270", {"start": v(-28.83, 6.7) * mm, "end": v(-28.81, 7.17) * mm});
            skLineSegment(sketch, "E271", {"start": v(-28.81, 7.17) * mm, "end": v(-28.36, 7.17) * mm});
            skLineSegment(sketch, "E272", {"start": v(-28.36, 7.17) * mm, "end": v(-28.36, 6.66) * mm});
            skLineSegment(sketch, "E273", {"start": v(-28.36, 6.66) * mm, "end": v(-28.21, 6.66) * mm});
            skLineSegment(sketch, "E274", {"start": v(-28.21, 6.66) * mm, "end": v(-28.21, 7.27) * mm});
            skLineSegment(sketch, "E275", {"start": v(-28.21, 7.27) * mm, "end": v(-28.21, 7.32) * mm});
            skLineSegment(sketch, "E276", {"start": v(-28.21, 7.32) * mm, "end": v(-28.98, 7.32) * mm});
            skLineSegment(sketch, "E277", {"start": v(-27.96, 7.3) * mm, "end": v(-27.96, 7.15) * mm});
            skLineSegment(sketch, "E278", {"start": v(-27.96, 7.15) * mm, "end": v(-27.66, 7.15) * mm});
            skLineSegment(sketch, "E279", {"start": v(-27.66, 7.15) * mm, "end": v(-27.66, 6.69) * mm});
            skLineSegment(sketch, "E280", {"start": v(-27.66, 6.69) * mm, "end": v(-27.48, 6.69) * mm});
            skLineSegment(sketch, "E281", {"start": v(-27.48, 6.69) * mm, "end": v(-27.48, 7.17) * mm});
            skLineSegment(sketch, "E282", {"start": v(-27.48, 7.17) * mm, "end": v(-27.2, 7.14) * mm});
            skLineSegment(sketch, "E283", {"start": v(-27.2, 7.14) * mm, "end": v(-27.23, 7.32) * mm});
            skLineSegment(sketch, "E284", {"start": v(-27.23, 7.32) * mm, "end": v(-27.96, 7.3) * mm});
            skLineSegment(sketch, "E285", {"start": v(-26.95, 6.68) * mm, "end": v(-26.95, 7.3) * mm});
            skLineSegment(sketch, "E286", {"start": v(-26.95, 7.3) * mm, "end": v(-26.17, 7.27) * mm});
            skLineSegment(sketch, "E287", {"start": v(-26.17, 7.27) * mm, "end": v(-26.17, 6.66) * mm});
            skLineSegment(sketch, "E288", {"start": v(-26.17, 6.66) * mm, "end": v(-26.36, 6.67) * mm});
            skLineSegment(sketch, "E289", {"start": v(-26.36, 6.67) * mm, "end": v(-26.35, 6.9) * mm});
            skLineSegment(sketch, "E290", {"start": v(-26.35, 6.9) * mm, "end": v(-26.84, 6.9) * mm});
            skLineSegment(sketch, "E291", {"start": v(-26.84, 6.9) * mm, "end": v(-26.83, 6.68) * mm});
            skLineSegment(sketch, "E292", {"start": v(-26.83, 6.68) * mm, "end": v(-26.95, 6.68) * mm});
            skLineSegment(sketch, "E293", {"start": v(-26.79, 7.14) * mm, "end": v(-26.79, 7.03) * mm});
            skLineSegment(sketch, "E294", {"start": v(-26.79, 7.03) * mm, "end": v(-26.35, 7.03) * mm});
            skLineSegment(sketch, "E295", {"start": v(-26.35, 7.03) * mm, "end": v(-26.34, 7.17) * mm});
            skLineSegment(sketch, "E296", {"start": v(-26.34, 7.17) * mm, "end": v(-26.79, 7.14) * mm});
            skLineSegment(sketch, "E297", {"start": v(-25.95, 7.26) * mm, "end": v(-25.95, 6.65) * mm});
            skLineSegment(sketch, "E298", {"start": v(-25.95, 6.65) * mm, "end": v(-25.18, 6.64) * mm});
            skLineSegment(sketch, "E299", {"start": v(-25.18, 6.64) * mm, "end": v(-25.2, 7.3) * mm});
            skLineSegment(sketch, "E300", {"start": v(-25.2, 7.3) * mm, "end": v(-25.31, 7.28) * mm});
            skLineSegment(sketch, "E301", {"start": v(-25.31, 7.28) * mm, "end": v(-25.32, 6.78) * mm});
            skLineSegment(sketch, "E302", {"start": v(-25.32, 6.78) * mm, "end": v(-25.79, 6.78) * mm});
            skLineSegment(sketch, "E303", {"start": v(-25.79, 6.78) * mm, "end": v(-25.8, 7.27) * mm});
            skLineSegment(sketch, "E304", {"start": v(-25.8, 7.27) * mm, "end": v(-25.95, 7.26) * mm});
            skLineSegment(sketch, "E305", {"start": v(-24.92, 7.26) * mm, "end": v(-24.9, 6.68) * mm});
            skLineSegment(sketch, "E306", {"start": v(-24.9, 6.68) * mm, "end": v(-24.73, 6.65) * mm});
            skLineSegment(sketch, "E307", {"start": v(-24.73, 6.65) * mm, "end": v(-24.75, 6.88) * mm});
            skLineSegment(sketch, "E308", {"start": v(-24.75, 6.88) * mm, "end": v(-24.3, 6.62) * mm});
            skLineSegment(sketch, "E309", {"start": v(-24.3, 6.62) * mm, "end": v(-24.15, 6.62) * mm});
            skLineSegment(sketch, "E310", {"start": v(-24.15, 6.62) * mm, "end": v(-24.15, 6.68) * mm});
            skLineSegment(sketch, "E311", {"start": v(-24.15, 6.68) * mm, "end": v(-24.4, 6.84) * mm});
            skLineSegment(sketch, "E312", {"start": v(-24.4, 6.84) * mm, "end": v(-24.15, 6.84) * mm});
            skLineSegment(sketch, "E313", {"start": v(-24.15, 6.84) * mm, "end": v(-24.16, 7.26) * mm});
            skLineSegment(sketch, "E314", {"start": v(-24.16, 7.26) * mm, "end": v(-24.92, 7.26) * mm});
            skLineSegment(sketch, "E315", {"start": v(-24.79, 7.15) * mm, "end": v(-24.78, 7.02) * mm});
            skLineSegment(sketch, "E316", {"start": v(-24.78, 7.02) * mm, "end": v(-24.26, 7.06) * mm});
            skLineSegment(sketch, "E317", {"start": v(-24.26, 7.06) * mm, "end": v(-24.31, 7.14) * mm});
            skLineSegment(sketch, "E318", {"start": v(-24.31, 7.14) * mm, "end": v(-24.79, 7.15) * mm});
            skLineSegment(sketch, "E319", {"start": v(-23.9, 7.26) * mm, "end": v(-23.9, 6.64) * mm});
            skLineSegment(sketch, "E320", {"start": v(-23.9, 6.64) * mm, "end": v(-23.76, 6.62) * mm});
            skLineSegment(sketch, "E321", {"start": v(-23.76, 6.62) * mm, "end": v(-23.78, 7.26) * mm});
            skLineSegment(sketch, "E322", {"start": v(-23.78, 7.26) * mm, "end": v(-23.9, 7.26) * mm});
            skLineSegment(sketch, "E323", {"start": v(-23.9, 7.26) * mm, "end": v(-23.9, 7.26) * mm});
            skLineSegment(sketch, "E324", {"start": v(-23.12, 7.4) * mm, "end": v(-23.1, 6.62) * mm});
            skLineSegment(sketch, "E325", {"start": v(-23.1, 6.62) * mm, "end": v(-22.16, 6.62) * mm});
            skLineSegment(sketch, "E326", {"start": v(-22.16, 6.62) * mm, "end": v(-22.16, 6.82) * mm});
            skLineSegment(sketch, "E327", {"start": v(-22.16, 6.82) * mm, "end": v(-22.9, 6.82) * mm});
            skLineSegment(sketch, "E328", {"start": v(-22.9, 6.82) * mm, "end": v(-22.93, 6.9) * mm});
            skLineSegment(sketch, "E329", {"start": v(-22.93, 6.9) * mm, "end": v(-22.21, 6.92) * mm});
            skLineSegment(sketch, "E330", {"start": v(-22.21, 6.92) * mm, "end": v(-22.17, 7.09) * mm});
            skLineSegment(sketch, "E331", {"start": v(-22.17, 7.09) * mm, "end": v(-22.9, 7.09) * mm});
            skLineSegment(sketch, "E332", {"start": v(-22.9, 7.09) * mm, "end": v(-22.92, 7.26) * mm});
            skLineSegment(sketch, "E333", {"start": v(-22.92, 7.26) * mm, "end": v(-22.15, 7.26) * mm});
            skLineSegment(sketch, "E334", {"start": v(-22.15, 7.26) * mm, "end": v(-22.15, 7.42) * mm});
            skLineSegment(sketch, "E335", {"start": v(-22.15, 7.42) * mm, "end": v(-23.12, 7.4) * mm});
            skLineSegment(sketch, "E336", {"start": v(-21.82, 7.19) * mm, "end": v(-21.61, 7.06) * mm});
            skLineSegment(sketch, "E337", {"start": v(-21.61, 7.06) * mm, "end": v(-21.61, 6.81) * mm});
            skLineSegment(sketch, "E338", {"start": v(-21.61, 6.81) * mm, "end": v(-21.85, 6.62) * mm});
            skLineSegment(sketch, "E339", {"start": v(-21.85, 6.62) * mm, "end": v(-21.71, 6.6) * mm});
            skLineSegment(sketch, "E340", {"start": v(-21.71, 6.6) * mm, "end": v(-21.48, 6.73) * mm});
            skLineSegment(sketch, "E341", {"start": v(-21.48, 6.73) * mm, "end": v(-21.23, 6.57) * mm});
            skLineSegment(sketch, "E342", {"start": v(-21.23, 6.57) * mm, "end": v(-21.1, 6.58) * mm});
            skLineSegment(sketch, "E343", {"start": v(-21.1, 6.58) * mm, "end": v(-21.07, 6.63) * mm});
            skLineSegment(sketch, "E344", {"start": v(-21.07, 6.63) * mm, "end": v(-21.37, 6.8) * mm});
            skLineSegment(sketch, "E345", {"start": v(-21.37, 6.8) * mm, "end": v(-21.38, 7.04) * mm});
            skLineSegment(sketch, "E346", {"start": v(-21.38, 7.04) * mm, "end": v(-21.15, 7.14) * mm});
            skLineSegment(sketch, "E347", {"start": v(-21.15, 7.14) * mm, "end": v(-21.08, 7.2) * mm});
            skLineSegment(sketch, "E348", {"start": v(-21.08, 7.2) * mm, "end": v(-21.11, 7.25) * mm});
            skLineSegment(sketch, "E349", {"start": v(-21.11, 7.25) * mm, "end": v(-21.26, 7.2) * mm});
            skLineSegment(sketch, "E350", {"start": v(-21.26, 7.2) * mm, "end": v(-21.49, 7.1) * mm});
            skLineSegment(sketch, "E351", {"start": v(-21.49, 7.1) * mm, "end": v(-21.73, 7.22) * mm});
            skLineSegment(sketch, "E352", {"start": v(-21.73, 7.22) * mm, "end": v(-21.82, 7.22) * mm});
            skLineSegment(sketch, "E353", {"start": v(-21.82, 7.22) * mm, "end": v(-21.82, 7.19) * mm});
            skLineSegment(sketch, "E354", {"start": v(-20.86, 7.19) * mm, "end": v(-20.84, 6.62) * mm});
            skLineSegment(sketch, "E355", {"start": v(-20.84, 6.62) * mm, "end": v(-20.68, 6.64) * mm});
            skLineSegment(sketch, "E356", {"start": v(-20.68, 6.64) * mm, "end": v(-20.68, 6.84) * mm});
            skLineSegment(sketch, "E357", {"start": v(-20.68, 6.84) * mm, "end": v(-20.1, 6.84) * mm});
            skLineSegment(sketch, "E358", {"start": v(-20.1, 6.84) * mm, "end": v(-20.1, 7.19) * mm});
            skLineSegment(sketch, "E359", {"start": v(-20.1, 7.19) * mm, "end": v(-20.86, 7.19) * mm});
            skLineSegment(sketch, "E360", {"start": v(-20.7, 7.08) * mm, "end": v(-20.7, 6.96) * mm});
            skLineSegment(sketch, "E361", {"start": v(-20.7, 6.96) * mm, "end": v(-20.23, 6.95) * mm});
            skLineSegment(sketch, "E362", {"start": v(-20.23, 6.95) * mm, "end": v(-20.24, 7.1) * mm});
            skLineSegment(sketch, "E363", {"start": v(-20.24, 7.1) * mm, "end": v(-20.7, 7.08) * mm});
            skLineSegment(sketch, "E364", {"start": v(-19.85, 7.14) * mm, "end": v(-19.82, 6.58) * mm});
            skLineSegment(sketch, "E365", {"start": v(-19.82, 6.58) * mm, "end": v(-19.05, 6.58) * mm});
            skLineSegment(sketch, "E366", {"start": v(-19.05, 6.58) * mm, "end": v(-19.07, 6.74) * mm});
            skLineSegment(sketch, "E367", {"start": v(-19.07, 6.74) * mm, "end": v(-19.69, 6.73) * mm});
            skLineSegment(sketch, "E368", {"start": v(-19.69, 6.73) * mm, "end": v(-19.69, 6.83) * mm});
            skLineSegment(sketch, "E369", {"start": v(-19.69, 6.83) * mm, "end": v(-19.06, 6.83) * mm});
            skLineSegment(sketch, "E370", {"start": v(-19.06, 6.83) * mm, "end": v(-19.06, 6.95) * mm});
            skLineSegment(sketch, "E371", {"start": v(-19.06, 6.95) * mm, "end": v(-19.64, 6.94) * mm});
            skLineSegment(sketch, "E372", {"start": v(-19.64, 6.94) * mm, "end": v(-19.65, 7.1) * mm});
            skLineSegment(sketch, "E373", {"start": v(-19.65, 7.1) * mm, "end": v(-19.03, 7.08) * mm});
            skLineSegment(sketch, "E374", {"start": v(-19.03, 7.08) * mm, "end": v(-19.07, 7.2) * mm});
            skLineSegment(sketch, "E375", {"start": v(-19.07, 7.2) * mm, "end": v(-19.87, 7.19) * mm});
            skLineSegment(sketch, "E376", {"start": v(-19.87, 7.19) * mm, "end": v(-19.85, 7.14) * mm});
            skLineSegment(sketch, "E377", {"start": v(-18.82, 7.18) * mm, "end": v(-18.8, 6.52) * mm});
            skLineSegment(sketch, "E378", {"start": v(-18.8, 6.52) * mm, "end": v(-18.26, 6.52) * mm});
            skLineSegment(sketch, "E379", {"start": v(-18.26, 6.52) * mm, "end": v(-18.1, 6.77) * mm});
            skLineSegment(sketch, "E380", {"start": v(-18.1, 6.77) * mm, "end": v(-18.08, 6.95) * mm});
            skLineSegment(sketch, "E381", {"start": v(-18.08, 6.95) * mm, "end": v(-18.23, 7.11) * mm});
            skLineSegment(sketch, "E382", {"start": v(-18.23, 7.11) * mm, "end": v(-18.82, 7.18) * mm});
            skLineSegment(sketch, "E383", {"start": v(-18.68, 7.01) * mm, "end": v(-18.66, 6.73) * mm});
            skLineSegment(sketch, "E384", {"start": v(-18.66, 6.73) * mm, "end": v(-18.48, 6.7) * mm});
            skLineSegment(sketch, "E385", {"start": v(-18.48, 6.7) * mm, "end": v(-18.3, 6.75) * mm});
            skLineSegment(sketch, "E386", {"start": v(-18.3, 6.75) * mm, "end": v(-18.2, 6.84) * mm});
            skLineSegment(sketch, "E387", {"start": v(-18.2, 6.84) * mm, "end": v(-18.26, 7) * mm});
            skLineSegment(sketch, "E388", {"start": v(-18.26, 7) * mm, "end": v(-18.63, 7.06) * mm});
            skLineSegment(sketch, "E389", {"start": v(-18.63, 7.06) * mm, "end": v(-18.68, 7.01) * mm});
            skLineSegment(sketch, "E390", {"start": v(-17.82, 7.15) * mm, "end": v(-17.82, 6.59) * mm});
            skLineSegment(sketch, "E391", {"start": v(-17.82, 6.59) * mm, "end": v(-17.67, 6.57) * mm});
            skLineSegment(sketch, "E392", {"start": v(-17.67, 6.57) * mm, "end": v(-17.67, 7.15) * mm});
            skLineSegment(sketch, "E393", {"start": v(-17.67, 7.15) * mm, "end": v(-17.82, 7.15) * mm});
            skLineSegment(sketch, "E394", {"start": v(-17.4, 7.15) * mm, "end": v(-17.4, 7.06) * mm});
            skLineSegment(sketch, "E395", {"start": v(-17.4, 7.06) * mm, "end": v(-17.13, 7.06) * mm});
            skLineSegment(sketch, "E396", {"start": v(-17.13, 7.06) * mm, "end": v(-17.1, 6.54) * mm});
            skLineSegment(sketch, "E397", {"start": v(-17.1, 6.54) * mm, "end": v(-16.97, 6.54) * mm});
            skLineSegment(sketch, "E398", {"start": v(-16.97, 6.54) * mm, "end": v(-16.97, 7.05) * mm});
            skLineSegment(sketch, "E399", {"start": v(-16.97, 7.05) * mm, "end": v(-16.7, 7.04) * mm});
            skLineSegment(sketch, "E400", {"start": v(-16.7, 7.04) * mm, "end": v(-16.7, 7.18) * mm});
            skLineSegment(sketch, "E401", {"start": v(-16.7, 7.18) * mm, "end": v(-17.4, 7.15) * mm});
            skLineSegment(sketch, "E402", {"start": v(-16.42, 7.15) * mm, "end": v(-16.42, 6.54) * mm});
            skLineSegment(sketch, "E403", {"start": v(-16.42, 6.54) * mm, "end": v(-16.25, 6.54) * mm});
            skLineSegment(sketch, "E404", {"start": v(-16.25, 6.54) * mm, "end": v(-16.23, 7.19) * mm});
            skLineSegment(sketch, "E405", {"start": v(-16.23, 7.19) * mm, "end": v(-16.42, 7.14) * mm});
            skLineSegment(sketch, "E406", {"start": v(-16, 7.15) * mm, "end": v(-16, 6.52) * mm});
            skLineSegment(sketch, "E407", {"start": v(-16, 6.52) * mm, "end": v(-15.25, 6.52) * mm});
            skLineSegment(sketch, "E408", {"start": v(-15.25, 6.52) * mm, "end": v(-15.25, 7.16) * mm});
            skLineSegment(sketch, "E409", {"start": v(-15.25, 7.16) * mm, "end": v(-16, 7.15) * mm});
            skLineSegment(sketch, "E410", {"start": v(-15.84, 7.04) * mm, "end": v(-15.84, 6.66) * mm});
            skLineSegment(sketch, "E411", {"start": v(-15.84, 6.66) * mm, "end": v(-15.41, 6.68) * mm});
            skLineSegment(sketch, "E412", {"start": v(-15.41, 6.68) * mm, "end": v(-15.44, 7.04) * mm});
            skLineSegment(sketch, "E413", {"start": v(-15.44, 7.04) * mm, "end": v(-15.84, 7.04) * mm});
            skLineSegment(sketch, "E414", {"start": v(-15.03, 6.53) * mm, "end": v(-14.82, 6.53) * mm});
            skLineSegment(sketch, "E415", {"start": v(-14.82, 6.53) * mm, "end": v(-14.82, 7.04) * mm});
            skLineSegment(sketch, "E416", {"start": v(-14.82, 7.04) * mm, "end": v(-14.36, 7.01) * mm});
            skLineSegment(sketch, "E417", {"start": v(-14.36, 7.01) * mm, "end": v(-14.36, 6.53) * mm});
            skLineSegment(sketch, "E418", {"start": v(-14.36, 6.53) * mm, "end": v(-14.25, 6.53) * mm});
            skLineSegment(sketch, "E419", {"start": v(-14.25, 6.53) * mm, "end": v(-14.25, 7.13) * mm});
            skLineSegment(sketch, "E420", {"start": v(-14.25, 7.13) * mm, "end": v(-15.01, 7.13) * mm});
            skLineSegment(sketch, "E421", {"start": v(-15.01, 7.13) * mm, "end": v(-15.03, 6.53) * mm});
            skLineSegment(sketch, "E422", {"start": v(-14, 6.63) * mm, "end": v(-14, 6.5) * mm});
            skLineSegment(sketch, "E423", {"start": v(-14, 6.5) * mm, "end": v(-13.24, 6.55) * mm});
            skLineSegment(sketch, "E424", {"start": v(-13.24, 6.55) * mm, "end": v(-13.24, 6.86) * mm});
            skLineSegment(sketch, "E425", {"start": v(-13.24, 6.86) * mm, "end": v(-13.82, 6.91) * mm});
            skLineSegment(sketch, "E426", {"start": v(-13.82, 6.91) * mm, "end": v(-13.82, 7) * mm});
            skLineSegment(sketch, "E427", {"start": v(-13.82, 7) * mm, "end": v(-13.22, 7.04) * mm});
            skLineSegment(sketch, "E428", {"start": v(-13.22, 7.04) * mm, "end": v(-13.22, 7.15) * mm});
            skLineSegment(sketch, "E429", {"start": v(-13.22, 7.15) * mm, "end": v(-13.97, 7.17) * mm});
            skLineSegment(sketch, "E430", {"start": v(-13.97, 7.17) * mm, "end": v(-13.97, 6.77) * mm});
            skLineSegment(sketch, "E431", {"start": v(-13.97, 6.77) * mm, "end": v(-13.43, 6.76) * mm});
            skLineSegment(sketch, "E432", {"start": v(-13.43, 6.76) * mm, "end": v(-13.38, 6.7) * mm});
            skLineSegment(sketch, "E433", {"start": v(-13.38, 6.7) * mm, "end": v(-13.38, 6.65) * mm});
            skLineSegment(sketch, "E434", {"start": v(-13.38, 6.65) * mm, "end": v(-14, 6.63) * mm});
            skLineSegment(sketch, "E435.top", {"start": v(-2.16, -7.5) * mm, "end": v(2.4, -7.5) * mm});
            skLineSegment(sketch, "E435.right", {"start": v(35.94, 30.6) * mm, "end": v(35.94, -7.5) * mm});
            skPoint(sketch, "E435.middle", {"position": v(16.89, 11.54) * mm});
            skLineSegment(sketch, "E436", {"start": v(-2.16, 30.6) * mm, "end": v(-2.16, 11.54) * mm});
            skLineSegment(sketch, "E437", {"start": v(-2.16, 11.54) * mm, "end": v(-2.16, -7.5) * mm});
            skLineSegment(sketch, "E438", {"start": v(-2.16, 21.07) * mm, "end": v(2.92, 21.07) * mm});
            skLineSegment(sketch, "E439", {"start": v(2.92, 21.07) * mm, "end": v(2.92, 26.15) * mm});
            skLineSegment(sketch, "E440", {"start": v(2.92, 26.15) * mm, "end": v(-2.16, 26.15) * mm});
            skLineSegment(sketch, "E441.MirrorCS", {"start": v(-2.16, 2.02) * mm, "end": v(2.92, 2.02) * mm});
            skLineSegment(sketch, "E442.MirrorCS", {"start": v(2.92, 2.02) * mm, "end": v(2.92, -3.06) * mm});
            skLineSegment(sketch, "E443.MirrorCS", {"start": v(2.92, -3.06) * mm, "end": v(-2.16, -3.06) * mm});
            skLineSegment(sketch, "E444.MirrorCS", {"start": v(30.86, 21.07) * mm, "end": v(30.86, 26.15) * mm});
            skLineSegment(sketch, "E445.MirrorCS", {"start": v(30.86, 26.15) * mm, "end": v(35.94, 26.15) * mm});
            skLineSegment(sketch, "E446.MirrorCS", {"start": v(35.94, 21.07) * mm, "end": v(30.86, 21.07) * mm});
            skLineSegment(sketch, "E447.MirrorCS", {"start": v(35.94, 2.02) * mm, "end": v(30.86, 2.02) * mm});
            skLineSegment(sketch, "E448.MirrorCS", {"start": v(30.86, 2.02) * mm, "end": v(30.86, -3.06) * mm});
            skLineSegment(sketch, "E449.MirrorCS", {"start": v(30.86, -3.06) * mm, "end": v(35.94, -3.06) * mm});
            skLineSegment(sketch, "E450", {"start": v(-2.16, 30.6) * mm, "end": v(2.4, 30.6) * mm});
            skLineSegment(sketch, "E451", {"start": v(16.89, 30.6) * mm, "end": v(26.41, 30.6) * mm});
            skLineSegment(sketch, "E452", {"start": v(7.36, 30.6) * mm, "end": v(7.36, 35.55) * mm});
            skLineSegment(sketch, "E453", {"start": v(7.36, 35.55) * mm, "end": v(2.4, 35.55) * mm});
            skLineSegment(sketch, "E454", {"start": v(2.4, 35.55) * mm, "end": v(2.4, 30.6) * mm});
            skLineSegment(sketch, "E455", {"start": v(26.41, 30.6) * mm, "end": v(26.41, 35.55) * mm});
            skLineSegment(sketch, "E456", {"start": v(26.41, 35.55) * mm, "end": v(31.37, 35.55) * mm});
            skLineSegment(sketch, "E457", {"start": v(31.37, 35.55) * mm, "end": v(31.37, 30.6) * mm});
            skLineSegment(sketch, "E458.MirrorCS", {"start": v(7.36, -7.5) * mm, "end": v(7.36, -12.46) * mm});
            skLineSegment(sketch, "E459.MirrorCS", {"start": v(7.36, -12.46) * mm, "end": v(2.4, -12.46) * mm});
            skLineSegment(sketch, "E460.MirrorCS", {"start": v(2.4, -12.46) * mm, "end": v(2.4, -7.5) * mm});
            skLineSegment(sketch, "E461.MirrorCS", {"start": v(26.41, -7.5) * mm, "end": v(26.41, -12.46) * mm});
            skLineSegment(sketch, "E462.MirrorCS", {"start": v(26.41, -12.46) * mm, "end": v(31.37, -12.46) * mm});
            skLineSegment(sketch, "E463.MirrorCS", {"start": v(31.37, -12.46) * mm, "end": v(31.37, -7.5) * mm});
            skLineSegment(sketch, "E464.trimOffspring", {"start": v(7.36, 30.6) * mm, "end": v(16.89, 30.6) * mm});
            skLineSegment(sketch, "E465.trimOffspring", {"start": v(31.37, 30.6) * mm, "end": v(35.94, 30.6) * mm});
            skLineSegment(sketch, "E466.trimOffspring", {"start": v(7.36, -7.5) * mm, "end": v(26.41, -7.5) * mm});
            skLineSegment(sketch, "E467.trimOffspring", {"start": v(31.37, -7.5) * mm, "end": v(35.94, -7.5) * mm});
            skPoint(sketch, "E468.endSnap0", {"position": v(28.72, 17.65) * mm});
            skLineSegment(sketch, "E469", {"start": v(6.13, 10.42) * mm, "end": v(6.13, 11.25) * mm});
            skLineSegment(sketch, "E470", {"start": v(6.13, 11.25) * mm, "end": v(7.26, 11.6) * mm});
            skLineSegment(sketch, "E471", {"start": v(7.26, 11.6) * mm, "end": v(8.73, 11.6) * mm});
            skLineSegment(sketch, "E472", {"start": v(8.73, 11.6) * mm, "end": v(9.66, 11.5) * mm});
            skLineSegment(sketch, "E473", {"start": v(9.66, 11.5) * mm, "end": v(10.47, 11.5) * mm});
            skLineSegment(sketch, "E474", {"start": v(10.47, 11.5) * mm, "end": v(10.95, 11.37) * mm});
            skLineSegment(sketch, "E475", {"start": v(10.95, 11.37) * mm, "end": v(10.95, 10.46) * mm});
            skLineSegment(sketch, "E476", {"start": v(10.95, 10.46) * mm, "end": v(10.47, 10.29) * mm});
            skLineSegment(sketch, "E477", {"start": v(10.47, 10.29) * mm, "end": v(10.08, 10.55) * mm});
            skLineSegment(sketch, "E478", {"start": v(10.08, 10.55) * mm, "end": v(9.78, 10.76) * mm});
            skLineSegment(sketch, "E479", {"start": v(9.78, 10.76) * mm, "end": v(7.1, 10.76) * mm});
            skLineSegment(sketch, "E480", {"start": v(7.1, 10.76) * mm, "end": v(7.1, 10.37) * mm});
            skLineSegment(sketch, "E481", {"start": v(7.1, 10.37) * mm, "end": v(6.52, 10.25) * mm});
            skLineSegment(sketch, "E482", {"start": v(6.52, 10.25) * mm, "end": v(6.13, 10.42) * mm});
            skLineSegment(sketch, "E483", {"start": v(4.87, 9.93) * mm, "end": v(6.13, 10.16) * mm});
            skLineSegment(sketch, "E484", {"start": v(6.13, 10.16) * mm, "end": v(7.08, 10.16) * mm});
            skLineSegment(sketch, "E485", {"start": v(7.08, 10.16) * mm, "end": v(8.5, 10.12) * mm});
            skLineSegment(sketch, "E486", {"start": v(8.5, 10.12) * mm, "end": v(10.13, 10.12) * mm});
            skLineSegment(sketch, "E487", {"start": v(10.13, 10.12) * mm, "end": v(11.78, 10.24) * mm});
            skLineSegment(sketch, "E488", {"start": v(11.78, 10.24) * mm, "end": v(11.9, 9.6) * mm});
            skLineSegment(sketch, "E489", {"start": v(11.9, 9.6) * mm, "end": v(6.89, 9.6) * mm});
            skLineSegment(sketch, "E490", {"start": v(6.89, 9.6) * mm, "end": v(5.84, 9.72) * mm});
            skLineSegment(sketch, "E491", {"start": v(5.84, 9.72) * mm, "end": v(5.04, 9.72) * mm});
            skLineSegment(sketch, "E492", {"start": v(5.04, 9.72) * mm, "end": v(4.87, 9.93) * mm});
            skLineSegment(sketch, "E493", {"start": v(6.13, 9.4) * mm, "end": v(6.13, 8.4) * mm});
            skLineSegment(sketch, "E494", {"start": v(6.13, 8.4) * mm, "end": v(6.13, 8.16) * mm});
            skLineSegment(sketch, "E495", {"start": v(6.13, 8.16) * mm, "end": v(6.89, 8.16) * mm});
            skLineSegment(sketch, "E496", {"start": v(6.89, 8.16) * mm, "end": v(7, 8.58) * mm});
            skLineSegment(sketch, "E497", {"start": v(7, 8.58) * mm, "end": v(6.89, 9.4) * mm});
            skLineSegment(sketch, "E498", {"start": v(6.89, 9.4) * mm, "end": v(6.13, 9.4) * mm});
            skLineSegment(sketch, "E499", {"start": v(10.21, 9.25) * mm, "end": v(10.21, 8.16) * mm});
            skLineSegment(sketch, "E500", {"start": v(10.21, 8.16) * mm, "end": v(10.82, 8.12) * mm});
            skLineSegment(sketch, "E501", {"start": v(10.82, 8.12) * mm, "end": v(10.97, 8.46) * mm});
            skLineSegment(sketch, "E502", {"start": v(10.97, 8.46) * mm, "end": v(10.97, 9.24) * mm});
            skLineSegment(sketch, "E503", {"start": v(10.97, 9.24) * mm, "end": v(10.21, 9.25) * mm});
            skLineSegment(sketch, "E504", {"start": v(12.38, 11.2) * mm, "end": v(12.38, 8.5) * mm});
            skLineSegment(sketch, "E505", {"start": v(12.38, 8.5) * mm, "end": v(13.14, 8.35) * mm});
            skLineSegment(sketch, "E506", {"start": v(13.14, 8.35) * mm, "end": v(14.52, 8.18) * mm});
            skLineSegment(sketch, "E507", {"start": v(14.52, 8.18) * mm, "end": v(15.68, 8.18) * mm});
            skLineSegment(sketch, "E508", {"start": v(15.68, 8.18) * mm, "end": v(16.45, 8.36) * mm});
            skLineSegment(sketch, "E509", {"start": v(16.45, 8.36) * mm, "end": v(16.87, 8.36) * mm});
            skLineSegment(sketch, "E510", {"start": v(16.87, 8.36) * mm, "end": v(16.97, 8.63) * mm});
            skLineSegment(sketch, "E511", {"start": v(16.97, 8.63) * mm, "end": v(16.97, 9.25) * mm});
            skLineSegment(sketch, "E512", {"start": v(16.97, 9.25) * mm, "end": v(15.97, 8.91) * mm});
            skLineSegment(sketch, "E513", {"start": v(15.97, 8.91) * mm, "end": v(15.3, 8.86) * mm});
            skLineSegment(sketch, "E514", {"start": v(15.3, 8.86) * mm, "end": v(14.83, 8.86) * mm});
            skLineSegment(sketch, "E515", {"start": v(14.83, 8.86) * mm, "end": v(13.68, 8.86) * mm});
            skLineSegment(sketch, "E516", {"start": v(13.68, 8.86) * mm, "end": v(13.03, 8.97) * mm});
            skLineSegment(sketch, "E517", {"start": v(13.03, 8.97) * mm, "end": v(13.03, 9.4) * mm});
            skLineSegment(sketch, "E518", {"start": v(13.03, 9.4) * mm, "end": v(13.03, 10.2) * mm});
            skLineSegment(sketch, "E519", {"start": v(13.03, 10.2) * mm, "end": v(13.03, 10.68) * mm});
            skLineSegment(sketch, "E520", {"start": v(13.03, 10.68) * mm, "end": v(13.95, 10.68) * mm});
            skLineSegment(sketch, "E521", {"start": v(13.95, 10.68) * mm, "end": v(14.49, 10.75) * mm});
            skLineSegment(sketch, "E522", {"start": v(14.49, 10.75) * mm, "end": v(15.62, 10.75) * mm});
            skLineSegment(sketch, "E523", {"start": v(15.62, 10.75) * mm, "end": v(16.54, 10.53) * mm});
            skLineSegment(sketch, "E524", {"start": v(16.54, 10.53) * mm, "end": v(16.93, 10.53) * mm});
            skLineSegment(sketch, "E525", {"start": v(16.93, 10.53) * mm, "end": v(17.03, 11.31) * mm});
            skLineSegment(sketch, "E526", {"start": v(17.03, 11.31) * mm, "end": v(15.4, 11.51) * mm});
            skLineSegment(sketch, "E527", {"start": v(15.4, 11.51) * mm, "end": v(13.84, 11.51) * mm});
            skLineSegment(sketch, "E528", {"start": v(13.84, 11.51) * mm, "end": v(12.55, 11.34) * mm});
            skLineSegment(sketch, "E529", {"start": v(12.55, 11.34) * mm, "end": v(12.38, 11.2) * mm});
            skLineSegment(sketch, "E530", {"start": v(17.2, 10.13) * mm, "end": v(17.2, 9.55) * mm});
            skLineSegment(sketch, "E531", {"start": v(17.2, 9.55) * mm, "end": v(22.17, 9.55) * mm});
            skLineSegment(sketch, "E532", {"start": v(22.17, 9.55) * mm, "end": v(23.22, 9.65) * mm});
            skLineSegment(sketch, "E533", {"start": v(23.22, 9.65) * mm, "end": v(24.13, 9.74) * mm});
            skLineSegment(sketch, "E534", {"start": v(24.13, 9.74) * mm, "end": v(24.13, 9.88) * mm});
            skLineSegment(sketch, "E535", {"start": v(24.13, 9.88) * mm, "end": v(23.15, 10.03) * mm});
            skLineSegment(sketch, "E536", {"start": v(23.15, 10.03) * mm, "end": v(21.72, 10.03) * mm});
            skLineSegment(sketch, "E537", {"start": v(21.72, 10.03) * mm, "end": v(19.96, 10.13) * mm});
            skLineSegment(sketch, "E538", {"start": v(19.96, 10.13) * mm, "end": v(17.2, 10.13) * mm});
            skLineSegment(sketch, "E539", {"start": v(18.12, 10.53) * mm, "end": v(18.2, 11.47) * mm});
            skLineSegment(sketch, "E540", {"start": v(18.2, 11.47) * mm, "end": v(22.8, 11.47) * mm});
            skLineSegment(sketch, "E541", {"start": v(22.8, 11.47) * mm, "end": v(22.94, 11.31) * mm});
            skLineSegment(sketch, "E542", {"start": v(22.94, 11.31) * mm, "end": v(23, 10.69) * mm});
            skLineSegment(sketch, "E543", {"start": v(23, 10.69) * mm, "end": v(22.78, 10.53) * mm});
            skLineSegment(sketch, "E544", {"start": v(22.78, 10.53) * mm, "end": v(19.9, 10.7) * mm});
            skLineSegment(sketch, "E545", {"start": v(19.9, 10.7) * mm, "end": v(19.08, 10.7) * mm});
            skLineSegment(sketch, "E546", {"start": v(19.08, 10.7) * mm, "end": v(19.02, 10.31) * mm});
            skLineSegment(sketch, "E547", {"start": v(19.02, 10.31) * mm, "end": v(18.46, 10.31) * mm});
            skLineSegment(sketch, "E548", {"start": v(18.46, 10.31) * mm, "end": v(18.1, 10.42) * mm});
            skLineSegment(sketch, "E549", {"start": v(18.1, 10.42) * mm, "end": v(18.12, 10.53) * mm});
            skLineSegment(sketch, "E550", {"start": v(18.12, 9.25) * mm, "end": v(18.9, 9.25) * mm});
            skLineSegment(sketch, "E551", {"start": v(18.9, 9.25) * mm, "end": v(19.04, 8.9) * mm});
            skLineSegment(sketch, "E552", {"start": v(19.04, 8.9) * mm, "end": v(19.72, 8.88) * mm});
            skLineSegment(sketch, "E553", {"start": v(19.72, 8.88) * mm, "end": v(22.84, 9) * mm});
            skLineSegment(sketch, "E554", {"start": v(22.84, 9) * mm, "end": v(22.91, 8.24) * mm});
            skLineSegment(sketch, "E555", {"start": v(22.91, 8.24) * mm, "end": v(18.37, 8.24) * mm});
            skLineSegment(sketch, "E556", {"start": v(18.37, 8.24) * mm, "end": v(18.12, 8.24) * mm});
            skLineSegment(sketch, "E557", {"start": v(18.12, 8.24) * mm, "end": v(18.08, 8.64) * mm});
            skLineSegment(sketch, "E558", {"start": v(18.08, 8.64) * mm, "end": v(18.12, 9.25) * mm});
            skLineSegment(sketch, "E559", {"start": v(23.62, 10.53) * mm, "end": v(25.3, 10.42) * mm});
            skLineSegment(sketch, "E560", {"start": v(25.3, 10.42) * mm, "end": v(25.83, 9.93) * mm});
            skLineSegment(sketch, "E561", {"start": v(25.83, 9.93) * mm, "end": v(27.18, 9.8) * mm});
            skLineSegment(sketch, "E562", {"start": v(27.18, 9.8) * mm, "end": v(25.65, 9.4) * mm});
            skLineSegment(sketch, "E563", {"start": v(25.65, 9.4) * mm, "end": v(25.36, 9.11) * mm});
            skLineSegment(sketch, "E564", {"start": v(25.36, 9.11) * mm, "end": v(23.55, 9.11) * mm});
            skLineSegment(sketch, "E565", {"start": v(23.55, 9.11) * mm, "end": v(24.42, 9.4) * mm});
            skLineSegment(sketch, "E566", {"start": v(24.42, 9.4) * mm, "end": v(24.52, 9.6) * mm});
            skLineSegment(sketch, "E567", {"start": v(24.52, 9.6) * mm, "end": v(24.36, 9.81) * mm});
            skLineSegment(sketch, "E568", {"start": v(24.36, 9.81) * mm, "end": v(24.52, 10.02) * mm});
            skLineSegment(sketch, "E569", {"start": v(24.52, 10.02) * mm, "end": v(24.17, 10.3) * mm});
            skLineSegment(sketch, "E570", {"start": v(24.17, 10.3) * mm, "end": v(23.59, 10.36) * mm});
            skLineSegment(sketch, "E571", {"start": v(23.59, 10.36) * mm, "end": v(23.45, 10.42) * mm});
            skLineSegment(sketch, "E572", {"start": v(23.45, 10.42) * mm, "end": v(23.62, 10.53) * mm});
            skLineSegment(sketch, "E573", {"start": v(22.99, 13.57) * mm, "end": v(23.85, 13.08) * mm});
            skLineSegment(sketch, "E574", {"start": v(23.85, 13.08) * mm, "end": v(24.83, 12.33) * mm});
            skLineSegment(sketch, "E575", {"start": v(24.83, 12.33) * mm, "end": v(25.95, 11.37) * mm});
            skLineSegment(sketch, "E576", {"start": v(25.95, 11.37) * mm, "end": v(27.04, 10.28) * mm});
            skLineSegment(sketch, "E577", {"start": v(27.04, 10.28) * mm, "end": v(27.95, 8.9) * mm});
            skLineSegment(sketch, "E578", {"start": v(27.95, 8.9) * mm, "end": v(28.68, 7.43) * mm});
            skLineSegment(sketch, "E579", {"start": v(28.68, 7.43) * mm, "end": v(28.27, 9.25) * mm});
            skLineSegment(sketch, "E580", {"start": v(28.27, 9.25) * mm, "end": v(27.73, 10.19) * mm});
            skLineSegment(sketch, "E581", {"start": v(27.73, 10.19) * mm, "end": v(27.24, 11.2) * mm});
            skLineSegment(sketch, "E582", {"start": v(27.24, 11.2) * mm, "end": v(26.02, 12.64) * mm});
            skLineSegment(sketch, "E583", {"start": v(26.02, 12.64) * mm, "end": v(25.11, 13.46) * mm});
            skLineSegment(sketch, "E584", {"start": v(25.11, 13.46) * mm, "end": v(23.98, 14.25) * mm});
            skLineSegment(sketch, "E585", {"start": v(23.98, 14.25) * mm, "end": v(23.23, 14.47) * mm});
            skLineSegment(sketch, "E586", {"start": v(23.23, 14.47) * mm, "end": v(22.99, 13.57) * mm});
            skLineSegment(sketch, "E587", {"start": v(22.99, 13.57) * mm, "end": v(22.43, 12.9) * mm});
            skLineSegment(sketch, "E588", {"start": v(22.43, 12.9) * mm, "end": v(21.64, 12.38) * mm});
            skLineSegment(sketch, "E589", {"start": v(21.64, 12.38) * mm, "end": v(20.18, 12.24) * mm});
            skLineSegment(sketch, "E590", {"start": v(20.18, 12.24) * mm, "end": v(19.8, 12.58) * mm});
            skLineSegment(sketch, "E591", {"start": v(19.8, 12.58) * mm, "end": v(19.24, 12.2) * mm});
            skLineSegment(sketch, "E592", {"start": v(19.24, 12.2) * mm, "end": v(18.65, 12.22) * mm});
            skLineSegment(sketch, "E593", {"start": v(18.65, 12.22) * mm, "end": v(18.23, 12.41) * mm});
            skLineSegment(sketch, "E594", {"start": v(18.23, 12.41) * mm, "end": v(18, 12.64) * mm});
            skLineSegment(sketch, "E595", {"start": v(18, 12.64) * mm, "end": v(17.9, 12.91) * mm});
            skLineSegment(sketch, "E596", {"start": v(17.9, 12.91) * mm, "end": v(18.04, 13.46) * mm});
            skLineSegment(sketch, "E597", {"start": v(18.04, 13.46) * mm, "end": v(18.26, 13.75) * mm});
            skLineSegment(sketch, "E598", {"start": v(18.26, 13.75) * mm, "end": v(18.44, 13.99) * mm});
            skLineSegment(sketch, "E599", {"start": v(18.44, 13.99) * mm, "end": v(18.78, 14.03) * mm});
            skLineSegment(sketch, "E600", {"start": v(18.78, 14.03) * mm, "end": v(19.23, 13.97) * mm});
            skLineSegment(sketch, "E601", {"start": v(19.23, 13.97) * mm, "end": v(19.56, 13.79) * mm});
            skLineSegment(sketch, "E602", {"start": v(19.56, 13.79) * mm, "end": v(19.85, 13.37) * mm});
            skLineSegment(sketch, "E603", {"start": v(19.85, 13.37) * mm, "end": v(19.88, 13.13) * mm});
            skLineSegment(sketch, "E604", {"start": v(19.88, 13.13) * mm, "end": v(19.88, 12.76) * mm});
            skLineSegment(sketch, "E605", {"start": v(19.88, 12.76) * mm, "end": v(19.8, 12.58) * mm});
            skLineSegment(sketch, "E606", {"start": v(18.86, 14.02) * mm, "end": v(18.94, 14.58) * mm});
            skLineSegment(sketch, "E607", {"start": v(18.94, 14.58) * mm, "end": v(19.23, 15.53) * mm});
            skLineSegment(sketch, "E608", {"start": v(19.23, 15.53) * mm, "end": v(19.67, 15.98) * mm});
            skLineSegment(sketch, "E609", {"start": v(19.67, 15.98) * mm, "end": v(20.22, 16.36) * mm});
            skLineSegment(sketch, "E610", {"start": v(20.22, 16.36) * mm, "end": v(21.12, 16.43) * mm});
            skLineSegment(sketch, "E611", {"start": v(21.12, 16.43) * mm, "end": v(21.78, 16.34) * mm});
            skLineSegment(sketch, "E612", {"start": v(21.78, 16.34) * mm, "end": v(22.45, 15.94) * mm});
            skLineSegment(sketch, "E613", {"start": v(22.45, 15.94) * mm, "end": v(22.98, 15.38) * mm});
            skLineSegment(sketch, "E614", {"start": v(22.98, 15.38) * mm, "end": v(23.18, 14.68) * mm});
            skLineSegment(sketch, "E615", {"start": v(23.18, 14.68) * mm, "end": v(23.23, 14.47) * mm});
            skLineSegment(sketch, "E616", {"start": v(19.23, 15.53) * mm, "end": v(18.82, 15.92) * mm});
            skLineSegment(sketch, "E617", {"start": v(18.82, 15.92) * mm, "end": v(17.97, 15.94) * mm});
            skLineSegment(sketch, "E618", {"start": v(17.97, 15.94) * mm, "end": v(16.07, 15.74) * mm});
            skLineSegment(sketch, "E619", {"start": v(16.07, 15.74) * mm, "end": v(14.9, 15.53) * mm});
            skLineSegment(sketch, "E620", {"start": v(14.9, 15.53) * mm, "end": v(13.8, 15.1) * mm});
            skLineSegment(sketch, "E621", {"start": v(13.8, 15.1) * mm, "end": v(12.8, 14.7) * mm});
            skLineSegment(sketch, "E622", {"start": v(12.8, 14.7) * mm, "end": v(11.09, 13.57) * mm});
            skLineSegment(sketch, "E623", {"start": v(11.09, 13.57) * mm, "end": v(9.8, 12.24) * mm});
            skLineSegment(sketch, "E624", {"start": v(9.8, 12.24) * mm, "end": v(9.61, 12.05) * mm});
            skLineSegment(sketch, "E625", {"start": v(9.61, 12.05) * mm, "end": v(10.88, 12.89) * mm});
            skLineSegment(sketch, "E626", {"start": v(10.88, 12.89) * mm, "end": v(11.95, 13.5) * mm});
            skLineSegment(sketch, "E627", {"start": v(11.95, 13.5) * mm, "end": v(13.44, 14.13) * mm});
            skLineSegment(sketch, "E628", {"start": v(13.44, 14.13) * mm, "end": v(14.88, 14.6) * mm});
            skLineSegment(sketch, "E629", {"start": v(14.88, 14.6) * mm, "end": v(17.13, 14.8) * mm});
            skLineSegment(sketch, "E630", {"start": v(17.13, 14.8) * mm, "end": v(19, 14.8) * mm});
            skLineSegment(sketch, "E631", {"start": v(4.86, 6.78) * mm, "end": v(4.86, 7.55) * mm});
            skLineSegment(sketch, "E632", {"start": v(4.86, 7.55) * mm, "end": v(5.83, 7.55) * mm});
            skLineSegment(sketch, "E633", {"start": v(5.83, 7.55) * mm, "end": v(5.83, 6.76) * mm});
            skLineSegment(sketch, "E634", {"start": v(5.83, 6.76) * mm, "end": v(5.65, 6.76) * mm});
            skLineSegment(sketch, "E635", {"start": v(5.65, 6.76) * mm, "end": v(5.65, 7.08) * mm});
            skLineSegment(sketch, "E636", {"start": v(5.65, 7.08) * mm, "end": v(5.07, 7.08) * mm});
            skLineSegment(sketch, "E637", {"start": v(5.07, 7.08) * mm, "end": v(5.07, 6.77) * mm});
            skLineSegment(sketch, "E638", {"start": v(5.07, 6.77) * mm, "end": v(4.86, 6.78) * mm});
            skLineSegment(sketch, "E639", {"start": v(5.05, 7.37) * mm, "end": v(5.05, 7.26) * mm});
            skLineSegment(sketch, "E640", {"start": v(5.05, 7.26) * mm, "end": v(5.63, 7.26) * mm});
            skLineSegment(sketch, "E641", {"start": v(5.63, 7.26) * mm, "end": v(5.63, 7.37) * mm});
            skLineSegment(sketch, "E642", {"start": v(5.63, 7.37) * mm, "end": v(5.05, 7.37) * mm});
            skLineSegment(sketch, "E643", {"start": v(6.13, 7.37) * mm, "end": v(6.13, 6.76) * mm});
            skLineSegment(sketch, "E644", {"start": v(6.13, 6.76) * mm, "end": v(6.9, 6.76) * mm});
            skLineSegment(sketch, "E645", {"start": v(6.9, 6.76) * mm, "end": v(6.9, 6.9) * mm});
            skLineSegment(sketch, "E646", {"start": v(6.9, 6.9) * mm, "end": v(6.3, 6.9) * mm});
            skLineSegment(sketch, "E647", {"start": v(6.3, 6.9) * mm, "end": v(6.3, 7.37) * mm});
            skLineSegment(sketch, "E648", {"start": v(6.3, 7.37) * mm, "end": v(6.13, 7.37) * mm});
            skLineSegment(sketch, "E649", {"start": v(7.15, 6.78) * mm, "end": v(7.15, 7.37) * mm});
            skLineSegment(sketch, "E650", {"start": v(7.15, 7.37) * mm, "end": v(7.92, 7.37) * mm});
            skLineSegment(sketch, "E651", {"start": v(7.92, 7.37) * mm, "end": v(7.92, 7) * mm});
            skLineSegment(sketch, "E652", {"start": v(7.92, 7) * mm, "end": v(7.3, 7) * mm});
            skLineSegment(sketch, "E653", {"start": v(7.3, 7) * mm, "end": v(7.3, 6.78) * mm});
            skLineSegment(sketch, "E654", {"start": v(7.3, 6.78) * mm, "end": v(7.15, 6.78) * mm});
            skLineSegment(sketch, "E655", {"start": v(7.3, 7.25) * mm, "end": v(7.3, 7.08) * mm});
            skLineSegment(sketch, "E656", {"start": v(7.3, 7.08) * mm, "end": v(7.76, 7.08) * mm});
            skLineSegment(sketch, "E657", {"start": v(7.76, 7.08) * mm, "end": v(7.76, 7.23) * mm});
            skLineSegment(sketch, "E658", {"start": v(7.76, 7.23) * mm, "end": v(7.3, 7.25) * mm});
            skLineSegment(sketch, "E659", {"start": v(8.16, 7.37) * mm, "end": v(8.16, 6.78) * mm});
            skLineSegment(sketch, "E660", {"start": v(8.16, 6.78) * mm, "end": v(8.32, 6.78) * mm});
            skLineSegment(sketch, "E661", {"start": v(8.32, 6.78) * mm, "end": v(8.3, 6.97) * mm});
            skLineSegment(sketch, "E662", {"start": v(8.3, 6.97) * mm, "end": v(8.8, 6.97) * mm});
            skLineSegment(sketch, "E663", {"start": v(8.8, 6.97) * mm, "end": v(8.78, 6.73) * mm});
            skLineSegment(sketch, "E664", {"start": v(8.78, 6.73) * mm, "end": v(8.94, 6.73) * mm});
            skLineSegment(sketch, "E665", {"start": v(8.94, 6.73) * mm, "end": v(8.94, 7.37) * mm});
            skLineSegment(sketch, "E666", {"start": v(8.94, 7.37) * mm, "end": v(8.75, 7.37) * mm});
            skLineSegment(sketch, "E667", {"start": v(8.75, 7.37) * mm, "end": v(8.75, 7.13) * mm});
            skLineSegment(sketch, "E668", {"start": v(8.75, 7.13) * mm, "end": v(8.36, 7.13) * mm});
            skLineSegment(sketch, "E669", {"start": v(8.36, 7.13) * mm, "end": v(8.36, 7.37) * mm});
            skLineSegment(sketch, "E670", {"start": v(8.36, 7.37) * mm, "end": v(8.16, 7.37) * mm});
            skLineSegment(sketch, "E671", {"start": v(9.19, 6.74) * mm, "end": v(9.19, 7.37) * mm});
            skLineSegment(sketch, "E672", {"start": v(9.19, 7.37) * mm, "end": v(9.96, 7.37) * mm});
            skLineSegment(sketch, "E673", {"start": v(9.96, 7.37) * mm, "end": v(9.96, 6.71) * mm});
            skLineSegment(sketch, "E674", {"start": v(9.96, 6.71) * mm, "end": v(9.81, 6.71) * mm});
            skLineSegment(sketch, "E675", {"start": v(9.81, 6.71) * mm, "end": v(9.82, 6.95) * mm});
            skLineSegment(sketch, "E676", {"start": v(9.82, 6.95) * mm, "end": v(9.35, 6.95) * mm});
            skLineSegment(sketch, "E677", {"start": v(9.35, 6.95) * mm, "end": v(9.37, 6.73) * mm});
            skLineSegment(sketch, "E678", {"start": v(9.37, 6.73) * mm, "end": v(9.19, 6.74) * mm});
            skLineSegment(sketch, "E679", {"start": v(9.35, 7.2) * mm, "end": v(9.35, 7.08) * mm});
            skLineSegment(sketch, "E680", {"start": v(9.35, 7.08) * mm, "end": v(9.8, 7.1) * mm});
            skLineSegment(sketch, "E681", {"start": v(9.8, 7.1) * mm, "end": v(9.78, 7.22) * mm});
            skLineSegment(sketch, "E682", {"start": v(9.78, 7.22) * mm, "end": v(9.35, 7.2) * mm});
            skLineSegment(sketch, "E683", {"start": v(10.57, 7.5) * mm, "end": v(10.57, 6.71) * mm});
            skLineSegment(sketch, "E684", {"start": v(10.57, 6.71) * mm, "end": v(11.55, 6.71) * mm});
            skLineSegment(sketch, "E685", {"start": v(11.55, 6.71) * mm, "end": v(11.55, 6.87) * mm});
            skLineSegment(sketch, "E686", {"start": v(11.55, 6.87) * mm, "end": v(10.82, 6.87) * mm});
            skLineSegment(sketch, "E687", {"start": v(10.82, 6.87) * mm, "end": v(10.82, 7.3) * mm});
            skLineSegment(sketch, "E688", {"start": v(10.82, 7.3) * mm, "end": v(11.55, 7.3) * mm});
            skLineSegment(sketch, "E689", {"start": v(11.55, 7.3) * mm, "end": v(11.55, 7.48) * mm});
            skLineSegment(sketch, "E690", {"start": v(11.55, 7.48) * mm, "end": v(10.57, 7.48) * mm});
            skLineSegment(sketch, "E691", {"start": v(11.84, 7.3) * mm, "end": v(11.84, 6.7) * mm});
            skLineSegment(sketch, "E692", {"start": v(11.84, 6.7) * mm, "end": v(12.58, 6.7) * mm});
            skLineSegment(sketch, "E693", {"start": v(12.58, 6.7) * mm, "end": v(12.6, 6.8) * mm});
            skLineSegment(sketch, "E694", {"start": v(12.6, 6.8) * mm, "end": v(12, 6.8) * mm});
            skLineSegment(sketch, "E695", {"start": v(12, 6.8) * mm, "end": v(12, 6.9) * mm});
            skLineSegment(sketch, "E696", {"start": v(12, 6.9) * mm, "end": v(12.6, 6.9) * mm});
            skLineSegment(sketch, "E697", {"start": v(12.6, 6.9) * mm, "end": v(12.6, 7.05) * mm});
            skLineSegment(sketch, "E698", {"start": v(12.6, 7.05) * mm, "end": v(12, 7.05) * mm});
            skLineSegment(sketch, "E699", {"start": v(12, 7.05) * mm, "end": v(12, 7.18) * mm});
            skLineSegment(sketch, "E700", {"start": v(12, 7.18) * mm, "end": v(12.63, 7.18) * mm});
            skLineSegment(sketch, "E701", {"start": v(12.63, 7.18) * mm, "end": v(12.63, 7.32) * mm});
            skLineSegment(sketch, "E702", {"start": v(12.63, 7.32) * mm, "end": v(11.84, 7.3) * mm});
            skLineSegment(sketch, "E703", {"start": v(12.85, 7.3) * mm, "end": v(12.85, 6.69) * mm});
            skLineSegment(sketch, "E704", {"start": v(12.85, 6.69) * mm, "end": v(13, 6.69) * mm});
            skLineSegment(sketch, "E705", {"start": v(13, 6.69) * mm, "end": v(13.02, 7.16) * mm});
            skLineSegment(sketch, "E706", {"start": v(13.02, 7.16) * mm, "end": v(13.47, 7.16) * mm});
            skLineSegment(sketch, "E707", {"start": v(13.47, 7.16) * mm, "end": v(13.47, 6.65) * mm});
            skLineSegment(sketch, "E708", {"start": v(13.47, 6.65) * mm, "end": v(13.62, 6.65) * mm});
            skLineSegment(sketch, "E709", {"start": v(13.62, 6.65) * mm, "end": v(13.62, 7.25) * mm});
            skLineSegment(sketch, "E710", {"start": v(13.62, 7.25) * mm, "end": v(13.62, 7.3) * mm});
            skLineSegment(sketch, "E711", {"start": v(13.62, 7.3) * mm, "end": v(12.85, 7.3) * mm});
            skLineSegment(sketch, "E712", {"start": v(13.87, 7.28) * mm, "end": v(13.87, 7.13) * mm});
            skLineSegment(sketch, "E713", {"start": v(13.87, 7.13) * mm, "end": v(14.17, 7.13) * mm});
            skLineSegment(sketch, "E714", {"start": v(14.17, 7.13) * mm, "end": v(14.17, 6.67) * mm});
            skLineSegment(sketch, "E715", {"start": v(14.17, 6.67) * mm, "end": v(14.35, 6.67) * mm});
            skLineSegment(sketch, "E716", {"start": v(14.35, 6.67) * mm, "end": v(14.35, 7.16) * mm});
            skLineSegment(sketch, "E717", {"start": v(14.35, 7.16) * mm, "end": v(14.63, 7.13) * mm});
            skLineSegment(sketch, "E718", {"start": v(14.63, 7.13) * mm, "end": v(14.6, 7.3) * mm});
            skLineSegment(sketch, "E719", {"start": v(14.6, 7.3) * mm, "end": v(13.87, 7.28) * mm});
            skLineSegment(sketch, "E720", {"start": v(14.88, 6.67) * mm, "end": v(14.88, 7.28) * mm});
            skLineSegment(sketch, "E721", {"start": v(14.88, 7.28) * mm, "end": v(15.66, 7.25) * mm});
            skLineSegment(sketch, "E722", {"start": v(15.66, 7.25) * mm, "end": v(15.66, 6.64) * mm});
            skLineSegment(sketch, "E723", {"start": v(15.66, 6.64) * mm, "end": v(15.47, 6.66) * mm});
            skLineSegment(sketch, "E724", {"start": v(15.47, 6.66) * mm, "end": v(15.48, 6.89) * mm});
            skLineSegment(sketch, "E725", {"start": v(15.48, 6.89) * mm, "end": v(15, 6.89) * mm});
            skLineSegment(sketch, "E726", {"start": v(15, 6.89) * mm, "end": v(15, 6.66) * mm});
            skLineSegment(sketch, "E727", {"start": v(15, 6.66) * mm, "end": v(14.88, 6.67) * mm});
            skLineSegment(sketch, "E728", {"start": v(15.05, 7.12) * mm, "end": v(15.05, 7.02) * mm});
            skLineSegment(sketch, "E729", {"start": v(15.05, 7.02) * mm, "end": v(15.48, 7.02) * mm});
            skLineSegment(sketch, "E730", {"start": v(15.48, 7.02) * mm, "end": v(15.5, 7.16) * mm});
            skLineSegment(sketch, "E731", {"start": v(15.5, 7.16) * mm, "end": v(15.05, 7.12) * mm});
            skLineSegment(sketch, "E732", {"start": v(15.88, 7.24) * mm, "end": v(15.88, 6.64) * mm});
            skLineSegment(sketch, "E733", {"start": v(15.88, 6.64) * mm, "end": v(16.66, 6.63) * mm});
            skLineSegment(sketch, "E734", {"start": v(16.66, 6.63) * mm, "end": v(16.63, 7.28) * mm});
            skLineSegment(sketch, "E735", {"start": v(16.63, 7.28) * mm, "end": v(16.52, 7.26) * mm});
            skLineSegment(sketch, "E736", {"start": v(16.52, 7.26) * mm, "end": v(16.5, 6.77) * mm});
            skLineSegment(sketch, "E737", {"start": v(16.5, 6.77) * mm, "end": v(16.05, 6.77) * mm});
            skLineSegment(sketch, "E738", {"start": v(16.05, 6.77) * mm, "end": v(16.03, 7.25) * mm});
            skLineSegment(sketch, "E739", {"start": v(16.03, 7.25) * mm, "end": v(15.88, 7.24) * mm});
            skLineSegment(sketch, "E740", {"start": v(16.9, 7.24) * mm, "end": v(16.93, 6.67) * mm});
            skLineSegment(sketch, "E741", {"start": v(16.93, 6.67) * mm, "end": v(17.1, 6.63) * mm});
            skLineSegment(sketch, "E742", {"start": v(17.1, 6.63) * mm, "end": v(17.08, 6.86) * mm});
            skLineSegment(sketch, "E743", {"start": v(17.08, 6.86) * mm, "end": v(17.53, 6.6) * mm});
            skLineSegment(sketch, "E744", {"start": v(17.53, 6.6) * mm, "end": v(17.69, 6.6) * mm});
            skLineSegment(sketch, "E745", {"start": v(17.69, 6.6) * mm, "end": v(17.68, 6.67) * mm});
            skLineSegment(sketch, "E746", {"start": v(17.68, 6.67) * mm, "end": v(17.43, 6.82) * mm});
            skLineSegment(sketch, "E747", {"start": v(17.43, 6.82) * mm, "end": v(17.69, 6.82) * mm});
            skLineSegment(sketch, "E748", {"start": v(17.69, 6.82) * mm, "end": v(17.67, 7.24) * mm});
            skLineSegment(sketch, "E749", {"start": v(17.67, 7.24) * mm, "end": v(16.9, 7.24) * mm});
            skLineSegment(sketch, "E750", {"start": v(17.05, 7.14) * mm, "end": v(17.05, 7) * mm});
            skLineSegment(sketch, "E751", {"start": v(17.05, 7) * mm, "end": v(17.58, 7.04) * mm});
            skLineSegment(sketch, "E752", {"start": v(17.58, 7.04) * mm, "end": v(17.52, 7.12) * mm});
            skLineSegment(sketch, "E753", {"start": v(17.52, 7.12) * mm, "end": v(17.05, 7.14) * mm});
            skLineSegment(sketch, "E754", {"start": v(17.93, 7.24) * mm, "end": v(17.93, 6.62) * mm});
            skLineSegment(sketch, "E755", {"start": v(17.93, 6.62) * mm, "end": v(18.08, 6.6) * mm});
            skLineSegment(sketch, "E756", {"start": v(18.08, 6.6) * mm, "end": v(18.05, 7.24) * mm});
            skLineSegment(sketch, "E757", {"start": v(18.05, 7.24) * mm, "end": v(17.94, 7.25) * mm});
            skLineSegment(sketch, "E758", {"start": v(17.94, 7.25) * mm, "end": v(17.93, 7.24) * mm});
            skLineSegment(sketch, "E759", {"start": v(18.71, 7.4) * mm, "end": v(18.74, 6.6) * mm});
            skLineSegment(sketch, "E760", {"start": v(18.74, 6.6) * mm, "end": v(19.68, 6.6) * mm});
            skLineSegment(sketch, "E761", {"start": v(19.68, 6.6) * mm, "end": v(19.67, 6.8) * mm});
            skLineSegment(sketch, "E762", {"start": v(19.67, 6.8) * mm, "end": v(18.93, 6.8) * mm});
            skLineSegment(sketch, "E763", {"start": v(18.93, 6.8) * mm, "end": v(18.9, 6.88) * mm});
            skLineSegment(sketch, "E764", {"start": v(18.9, 6.88) * mm, "end": v(19.62, 6.9) * mm});
            skLineSegment(sketch, "E765", {"start": v(19.62, 6.9) * mm, "end": v(19.66, 7.07) * mm});
            skLineSegment(sketch, "E766", {"start": v(19.66, 7.07) * mm, "end": v(18.93, 7.07) * mm});
            skLineSegment(sketch, "E767", {"start": v(18.93, 7.07) * mm, "end": v(18.91, 7.25) * mm});
            skLineSegment(sketch, "E768", {"start": v(18.91, 7.25) * mm, "end": v(19.68, 7.24) * mm});
            skLineSegment(sketch, "E769", {"start": v(19.68, 7.24) * mm, "end": v(19.68, 7.4) * mm});
            skLineSegment(sketch, "E770", {"start": v(19.68, 7.4) * mm, "end": v(18.71, 7.4) * mm});
            skLineSegment(sketch, "E771", {"start": v(20, 7.17) * mm, "end": v(20.22, 7.04) * mm});
            skLineSegment(sketch, "E772", {"start": v(20.22, 7.04) * mm, "end": v(20.22, 6.8) * mm});
            skLineSegment(sketch, "E773", {"start": v(20.22, 6.8) * mm, "end": v(19.98, 6.6) * mm});
            skLineSegment(sketch, "E774", {"start": v(19.98, 6.6) * mm, "end": v(20.12, 6.6) * mm});
            skLineSegment(sketch, "E775", {"start": v(20.12, 6.6) * mm, "end": v(20.36, 6.72) * mm});
            skLineSegment(sketch, "E776", {"start": v(20.36, 6.72) * mm, "end": v(20.6, 6.55) * mm});
            skLineSegment(sketch, "E777", {"start": v(20.6, 6.55) * mm, "end": v(20.73, 6.57) * mm});
            skLineSegment(sketch, "E778", {"start": v(20.73, 6.57) * mm, "end": v(20.77, 6.61) * mm});
            skLineSegment(sketch, "E779", {"start": v(20.77, 6.61) * mm, "end": v(20.47, 6.79) * mm});
            skLineSegment(sketch, "E780", {"start": v(20.47, 6.79) * mm, "end": v(20.46, 7.02) * mm});
            skLineSegment(sketch, "E781", {"start": v(20.46, 7.02) * mm, "end": v(20.68, 7.12) * mm});
            skLineSegment(sketch, "E782", {"start": v(20.68, 7.12) * mm, "end": v(20.76, 7.19) * mm});
            skLineSegment(sketch, "E783", {"start": v(20.76, 7.19) * mm, "end": v(20.72, 7.23) * mm});
            skLineSegment(sketch, "E784", {"start": v(20.72, 7.23) * mm, "end": v(20.57, 7.19) * mm});
            skLineSegment(sketch, "E785", {"start": v(20.57, 7.19) * mm, "end": v(20.34, 7.08) * mm});
            skLineSegment(sketch, "E786", {"start": v(20.34, 7.08) * mm, "end": v(20.1, 7.2) * mm});
            skLineSegment(sketch, "E787", {"start": v(20.1, 7.2) * mm, "end": v(20.01, 7.2) * mm});
            skLineSegment(sketch, "E788", {"start": v(20.01, 7.2) * mm, "end": v(20, 7.17) * mm});
            skLineSegment(sketch, "E789", {"start": v(20.97, 7.17) * mm, "end": v(21, 6.6) * mm});
            skLineSegment(sketch, "E790", {"start": v(21, 6.6) * mm, "end": v(21.15, 6.62) * mm});
            skLineSegment(sketch, "E791", {"start": v(21.15, 6.62) * mm, "end": v(21.15, 6.83) * mm});
            skLineSegment(sketch, "E792", {"start": v(21.15, 6.83) * mm, "end": v(21.74, 6.83) * mm});
            skLineSegment(sketch, "E793", {"start": v(21.74, 6.83) * mm, "end": v(21.74, 7.17) * mm});
            skLineSegment(sketch, "E794", {"start": v(21.74, 7.17) * mm, "end": v(20.97, 7.17) * mm});
            skLineSegment(sketch, "E795", {"start": v(21.12, 7.06) * mm, "end": v(21.13, 6.95) * mm});
            skLineSegment(sketch, "E796", {"start": v(21.13, 6.95) * mm, "end": v(21.6, 6.93) * mm});
            skLineSegment(sketch, "E797", {"start": v(21.6, 6.93) * mm, "end": v(21.6, 7.07) * mm});
            skLineSegment(sketch, "E798", {"start": v(21.6, 7.07) * mm, "end": v(21.12, 7.06) * mm});
            skLineSegment(sketch, "E799", {"start": v(21.99, 7.12) * mm, "end": v(22, 6.56) * mm});
            skLineSegment(sketch, "E800", {"start": v(22, 6.56) * mm, "end": v(22.78, 6.56) * mm});
            skLineSegment(sketch, "E801", {"start": v(22.78, 6.56) * mm, "end": v(22.76, 6.72) * mm});
            skLineSegment(sketch, "E802", {"start": v(22.76, 6.72) * mm, "end": v(22.15, 6.71) * mm});
            skLineSegment(sketch, "E803", {"start": v(22.15, 6.71) * mm, "end": v(22.15, 6.82) * mm});
            skLineSegment(sketch, "E804", {"start": v(22.15, 6.82) * mm, "end": v(22.77, 6.81) * mm});
            skLineSegment(sketch, "E805", {"start": v(22.77, 6.81) * mm, "end": v(22.77, 6.93) * mm});
            skLineSegment(sketch, "E806", {"start": v(22.77, 6.93) * mm, "end": v(22.2, 6.93) * mm});
            skLineSegment(sketch, "E807", {"start": v(22.2, 6.93) * mm, "end": v(22.18, 7.1) * mm});
            skLineSegment(sketch, "E808", {"start": v(22.18, 7.1) * mm, "end": v(22.8, 7.06) * mm});
            skLineSegment(sketch, "E809", {"start": v(22.8, 7.06) * mm, "end": v(22.76, 7.19) * mm});
            skLineSegment(sketch, "E810", {"start": v(22.76, 7.19) * mm, "end": v(21.96, 7.17) * mm});
            skLineSegment(sketch, "E811", {"start": v(21.96, 7.17) * mm, "end": v(21.99, 7.12) * mm});
            skLineSegment(sketch, "E812", {"start": v(23, 7.16) * mm, "end": v(23.04, 6.5) * mm});
            skLineSegment(sketch, "E813", {"start": v(23.04, 6.5) * mm, "end": v(23.58, 6.5) * mm});
            skLineSegment(sketch, "E814", {"start": v(23.58, 6.5) * mm, "end": v(23.73, 6.75) * mm});
            skLineSegment(sketch, "E815", {"start": v(23.73, 6.75) * mm, "end": v(23.76, 6.94) * mm});
            skLineSegment(sketch, "E816", {"start": v(23.76, 6.94) * mm, "end": v(23.6, 7.1) * mm});
            skLineSegment(sketch, "E817", {"start": v(23.6, 7.1) * mm, "end": v(23, 7.16) * mm});
            skLineSegment(sketch, "E818", {"start": v(23.16, 7) * mm, "end": v(23.17, 6.72) * mm});
            skLineSegment(sketch, "E819", {"start": v(23.17, 6.72) * mm, "end": v(23.35, 6.69) * mm});
            skLineSegment(sketch, "E820", {"start": v(23.35, 6.69) * mm, "end": v(23.54, 6.74) * mm});
            skLineSegment(sketch, "E821", {"start": v(23.54, 6.74) * mm, "end": v(23.63, 6.82) * mm});
            skLineSegment(sketch, "E822", {"start": v(23.63, 6.82) * mm, "end": v(23.58, 6.98) * mm});
            skLineSegment(sketch, "E823", {"start": v(23.58, 6.98) * mm, "end": v(23.2, 7.04) * mm});
            skLineSegment(sketch, "E824", {"start": v(23.2, 7.04) * mm, "end": v(23.16, 7) * mm});
            skLineSegment(sketch, "E825", {"start": v(24, 7.13) * mm, "end": v(24, 6.57) * mm});
            skLineSegment(sketch, "E826", {"start": v(24, 6.57) * mm, "end": v(24.16, 6.56) * mm});
            skLineSegment(sketch, "E827", {"start": v(24.16, 6.56) * mm, "end": v(24.16, 7.14) * mm});
            skLineSegment(sketch, "E828", {"start": v(24.16, 7.14) * mm, "end": v(24, 7.13) * mm});
            skLineSegment(sketch, "E829", {"start": v(24.44, 7.13) * mm, "end": v(24.44, 7.05) * mm});
            skLineSegment(sketch, "E830", {"start": v(24.44, 7.05) * mm, "end": v(24.7, 7.05) * mm});
            skLineSegment(sketch, "E831", {"start": v(24.7, 7.05) * mm, "end": v(24.74, 6.52) * mm});
            skLineSegment(sketch, "E832", {"start": v(24.74, 6.52) * mm, "end": v(24.86, 6.52) * mm});
            skLineSegment(sketch, "E833", {"start": v(24.86, 6.52) * mm, "end": v(24.86, 7.04) * mm});
            skLineSegment(sketch, "E834", {"start": v(24.86, 7.04) * mm, "end": v(25.13, 7.02) * mm});
            skLineSegment(sketch, "E835", {"start": v(25.13, 7.02) * mm, "end": v(25.13, 7.16) * mm});
            skLineSegment(sketch, "E836", {"start": v(25.13, 7.16) * mm, "end": v(24.44, 7.13) * mm});
            skLineSegment(sketch, "E837", {"start": v(25.42, 7.13) * mm, "end": v(25.42, 6.52) * mm});
            skLineSegment(sketch, "E838", {"start": v(25.42, 6.52) * mm, "end": v(25.58, 6.52) * mm});
            skLineSegment(sketch, "E839", {"start": v(25.58, 6.52) * mm, "end": v(25.6, 7.17) * mm});
            skLineSegment(sketch, "E840", {"start": v(25.6, 7.17) * mm, "end": v(25.42, 7.12) * mm});
            skLineSegment(sketch, "E841", {"start": v(25.84, 7.13) * mm, "end": v(25.84, 6.5) * mm});
            skLineSegment(sketch, "E842", {"start": v(25.84, 6.5) * mm, "end": v(26.59, 6.5) * mm});
            skLineSegment(sketch, "E843", {"start": v(26.59, 6.5) * mm, "end": v(26.58, 7.14) * mm});
            skLineSegment(sketch, "E844", {"start": v(26.58, 7.14) * mm, "end": v(25.84, 7.13) * mm});
            skLineSegment(sketch, "E845", {"start": v(26, 7.02) * mm, "end": v(26, 6.65) * mm});
            skLineSegment(sketch, "E846", {"start": v(26, 6.65) * mm, "end": v(26.42, 6.66) * mm});
            skLineSegment(sketch, "E847", {"start": v(26.42, 6.66) * mm, "end": v(26.4, 7.03) * mm});
            skLineSegment(sketch, "E848", {"start": v(26.4, 7.03) * mm, "end": v(26, 7.02) * mm});
            skLineSegment(sketch, "E849", {"start": v(26.8, 6.51) * mm, "end": v(27.01, 6.51) * mm});
            skLineSegment(sketch, "E850", {"start": v(27.01, 6.51) * mm, "end": v(27.01, 7.02) * mm});
            skLineSegment(sketch, "E851", {"start": v(27.01, 7.02) * mm, "end": v(27.47, 7) * mm});
            skLineSegment(sketch, "E852", {"start": v(27.47, 7) * mm, "end": v(27.47, 6.51) * mm});
            skLineSegment(sketch, "E853", {"start": v(27.47, 6.51) * mm, "end": v(27.59, 6.51) * mm});
            skLineSegment(sketch, "E854", {"start": v(27.59, 6.51) * mm, "end": v(27.59, 7.12) * mm});
            skLineSegment(sketch, "E855", {"start": v(27.59, 7.12) * mm, "end": v(26.82, 7.12) * mm});
            skLineSegment(sketch, "E856", {"start": v(26.82, 7.12) * mm, "end": v(26.8, 6.51) * mm});
            skLineSegment(sketch, "E857", {"start": v(27.83, 6.62) * mm, "end": v(27.83, 6.48) * mm});
            skLineSegment(sketch, "E858", {"start": v(27.83, 6.48) * mm, "end": v(28.6, 6.53) * mm});
            skLineSegment(sketch, "E859", {"start": v(28.6, 6.53) * mm, "end": v(28.6, 6.84) * mm});
            skLineSegment(sketch, "E860", {"start": v(28.6, 6.84) * mm, "end": v(28.02, 6.9) * mm});
            skLineSegment(sketch, "E861", {"start": v(28.02, 6.9) * mm, "end": v(28.02, 6.98) * mm});
            skLineSegment(sketch, "E862", {"start": v(28.02, 6.98) * mm, "end": v(28.62, 7.02) * mm});
            skLineSegment(sketch, "E863", {"start": v(28.62, 7.02) * mm, "end": v(28.61, 7.14) * mm});
            skLineSegment(sketch, "E864", {"start": v(28.61, 7.14) * mm, "end": v(27.87, 7.15) * mm});
            skLineSegment(sketch, "E865", {"start": v(27.87, 7.15) * mm, "end": v(27.87, 6.76) * mm});
            skLineSegment(sketch, "E866", {"start": v(27.87, 6.76) * mm, "end": v(28.4, 6.75) * mm});
            skLineSegment(sketch, "E867", {"start": v(28.4, 6.75) * mm, "end": v(28.45, 6.68) * mm});
            skLineSegment(sketch, "E868", {"start": v(28.45, 6.68) * mm, "end": v(28.45, 6.63) * mm});
            skLineSegment(sketch, "E869", {"start": v(28.45, 6.63) * mm, "end": v(27.83, 6.62) * mm});
            skSolve(sketch);
        }
        {
            var Q0;
            {var subQ15=sQuery(id+"F0.wireOp",EDGE,"E0.top");Q0=makeQuery(id+"F0.imprint","IMPRINT",FACE,{"disambiguationData":[TD([[makeQuery(id+"F0.imprint","IMPRINT",EDGE,{"derivedFrom":subQ15}),1.0]])]});}
            var Q1;
            {var subQ15=sQuery(id+"F0.wireOp",EDGE,"E435.top");Q1=makeQuery(id+"F0.imprint","IMPRINT",FACE,{"disambiguationData":[TD([[makeQuery(id+"F0.imprint","IMPRINT",EDGE,{"derivedFrom":subQ15}),1.0]])]});}
            extrude(context, id + "F1", {"entities" : qUnion([Q0, Q1]), "depth" : 5.08 * mm, "offsetDistance" : 25 * mm});
        }
    });
